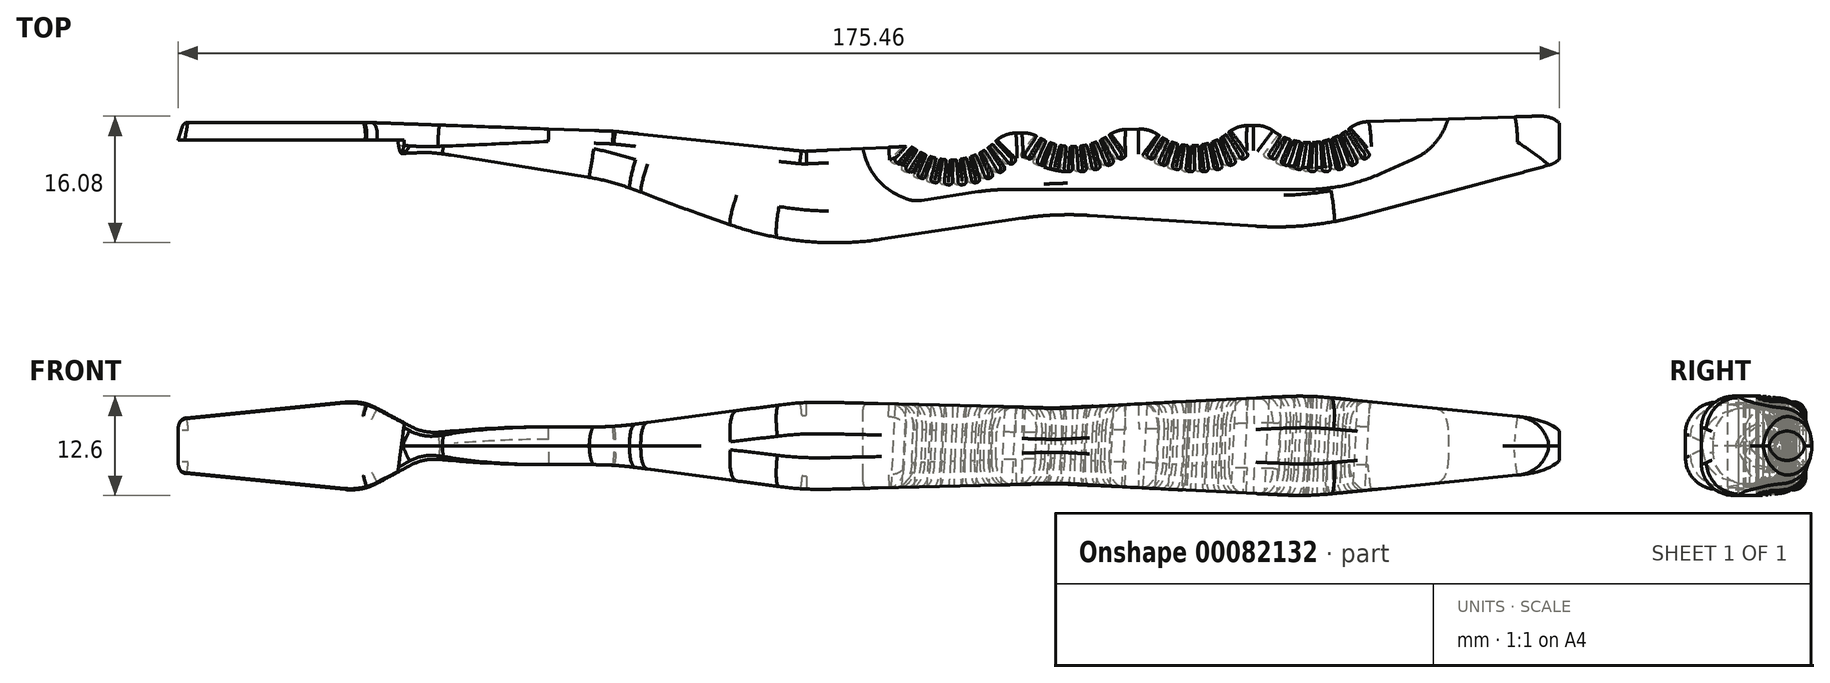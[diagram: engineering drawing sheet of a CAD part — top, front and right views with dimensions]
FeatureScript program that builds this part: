
annotation { "Feature Type Name" : "Feature", "Feature Type Description" : "" }
export const myFeature = defineFeature(function(context is Context, id is Id, definition is map)
    precondition{}
    {
        {
            var Q0;
            Q0=qCreatedBy(makeId("Front.planeOp"),FACE);
            var sketch = newSketch(context, id + "F0", { "sketchPlane" : qUnion([Q0])});
            skLineSegment(sketch, "E0", {"start": v(0, 0) * mm, "end": v(-220, 0) * mm, "construction": true});
            skLineSegment(sketch, "E1", {"start": v(-220, 0) * mm, "end": v(-220, 5) * mm});
            skLineSegment(sketch, "E2", {"start": v(-190, 0) * mm, "end": v(-190, 8) * mm, "construction": true});
            skLineSegment(sketch, "E3", {"start": v(-180, 0) * mm, "end": v(-180, 3) * mm, "construction": true});
            skLineSegment(sketch, "E4", {"start": v(-150, 0) * mm, "end": v(-150, 3) * mm, "construction": true});
            skLineSegment(sketch, "E5", {"start": v(-120, 0) * mm, "end": v(-120, 7) * mm, "construction": true});
            skLineSegment(sketch, "E6", {"start": v(-80, 0) * mm, "end": v(-80, 6) * mm, "construction": true});
            skLineSegment(sketch, "E7", {"start": v(-40, 0) * mm, "end": v(-40, 8) * mm, "construction": true});
            skLineSegment(sketch, "E8", {"start": v(0, 0) * mm, "end": v(0, 4) * mm});
            skLineSegment(sketch, "E9", {"start": v(0, 4) * mm, "end": v(-40, 8) * mm});
            skLineSegment(sketch, "E10", {"start": v(-40, 8) * mm, "end": v(-80, 6) * mm});
            skLineSegment(sketch, "E11", {"start": v(-80, 6) * mm, "end": v(-120, 7) * mm});
            skLineSegment(sketch, "E12", {"start": v(-120, 7) * mm, "end": v(-150, 3) * mm});
            skLineSegment(sketch, "E13", {"start": v(-150, 3) * mm, "end": v(-180, 3) * mm});
            skLineSegment(sketch, "E14", {"start": v(-180, 3) * mm, "end": v(-190, 8) * mm});
            skLineSegment(sketch, "E15", {"start": v(-190, 8) * mm, "end": v(-220, 5) * mm});
            skLineSegment(sketch, "E16.MirrorCS", {"start": v(0, 0) * mm, "end": v(0, -4) * mm});
            skLineSegment(sketch, "E17.MirrorCS", {"start": v(-220, 0) * mm, "end": v(-220, -5) * mm});
            skLineSegment(sketch, "E18.MirrorCS", {"start": v(-190, -8) * mm, "end": v(-220, -5) * mm});
            skLineSegment(sketch, "E19.MirrorCS", {"start": v(-180, -3) * mm, "end": v(-190, -8) * mm});
            skLineSegment(sketch, "E20.MirrorCS", {"start": v(-150, -3) * mm, "end": v(-180, -3) * mm});
            skLineSegment(sketch, "E21.MirrorCS", {"start": v(-120, -7) * mm, "end": v(-150, -3) * mm});
            skLineSegment(sketch, "E22.MirrorCS", {"start": v(-80, -6) * mm, "end": v(-120, -7) * mm});
            skLineSegment(sketch, "E23.MirrorCS", {"start": v(0, -4) * mm, "end": v(-40, -8) * mm});
            skLineSegment(sketch, "E24.MirrorCS", {"start": v(-40, -8) * mm, "end": v(-80, -6) * mm});
            skSolve(sketch);
        }
        {
            var Q0;
            Q0=makeQuery(id+"F0.imprint","IMPRINT",FACE,{"disambiguationData":[TD([[makeQuery(id+"F0.imprint","IMPRINT",EDGE,{"derivedFrom":sQuery(id+"F0.wireOp",EDGE,"E1")}),-1.0]])]});
            extrude(context, id + "F1", {"entities" : qUnion([Q0]), "depth" : 25 * mm});
        }
        {
            var Q0;
            Q0=makeQuery(id+"F1.opExtrude","SWEPT_FACE",FACE,{"disambiguationData":[OSD([sQuery(id+"F0.wireOp",EDGE,"E20.MirrorCS")])]});
            var sketch = newSketch(context, id + "F2", { "sketchPlane" : qUnion([Q0])});
            skLineSegment(sketch, "E25.0", {"start": v(-190, 0) * mm, "end": v(-220, 0) * mm, "construction": true});
            skLineSegment(sketch, "E25.4", {"start": v(-80, 0) * mm, "end": v(-120, 0) * mm, "construction": true});
            skLineSegment(sketch, "E25.5", {"start": v(-40, 0) * mm, "end": v(-80, 0) * mm, "construction": true});
            skLineSegment(sketch, "E25.6", {"start": v(0, 0) * mm, "end": v(-40, 0) * mm, "construction": true});
            skLineSegment(sketch, "E26", {"start": v(-220, 7.68) * mm, "end": v(-218.46, 2.68) * mm});
            skLineSegment(sketch, "E27", {"start": v(-218.46, 2.68) * mm, "end": v(-190, 2.68) * mm});
            skLineSegment(sketch, "E28", {"start": v(-119.9, 7.3) * mm, "end": v(-102.9, 6.47) * mm});
            skLineSegment(sketch, "E29", {"start": v(-119.9, 23.1) * mm, "end": v(-80, 17.11) * mm});
            skLineSegment(sketch, "E30", {"start": v(-80, 17.11) * mm, "end": v(-40, 19.71) * mm});
            skLineSegment(sketch, "E31", {"start": v(-40, 19.71) * mm, "end": v(0, 9.1) * mm});
            skLineSegment(sketch, "E32", {"start": v(0, 9.1) * mm, "end": v(0, 1.58) * mm});
            skArc(sketch, "E33", {"start": v(-88.51, 4.45) * mm, "mid": v(-95.27, 8.57) * mm, "end": v(-102.9, 6.47) * mm});
            skArc(sketch, "E34", {"start": v(-32.26, 2.63) * mm, "mid": v(-39.34, 5.9) * mm, "end": v(-46.62, 3.1) * mm});
            skLineSegment(sketch, "E35", {"start": v(-88.51, 4.45) * mm, "end": v(-83.73, 4.3) * mm});
            skLineSegment(sketch, "E36", {"start": v(-70.5, 3.87) * mm, "end": v(-64.85, 3.69) * mm});
            skArc(sketch, "E37.trimOffspring", {"start": v(-70.5, 3.87) * mm, "mid": v(-77.03, 6.54) * mm, "end": v(-83.73, 4.3) * mm});
            skLineSegment(sketch, "E38.trimOffspring", {"start": v(-51.47, 3.25) * mm, "end": v(-46.62, 3.1) * mm});
            skLineSegment(sketch, "E39.trimOffspring", {"start": v(-32.26, 2.63) * mm, "end": v(0, 1.58) * mm});
            skArc(sketch, "E40.trimOffspring", {"start": v(-51.47, 3.25) * mm, "mid": v(-58.07, 6.39) * mm, "end": v(-64.85, 3.69) * mm});
            skPoint(sketch, "E41.center.orphan", {"position": v(-77.66, -2.25) * mm});
            skPoint(sketch, "E42.center.orphan", {"position": v(-58.66, -3.17) * mm});
            skLineSegment(sketch, "E43.top", {"start": v(-229.41, 31.75) * mm, "end": v(15.55, 31.75) * mm});
            skLineSegment(sketch, "E43.left", {"start": v(-229.41, -17.07) * mm, "end": v(-229.41, 31.75) * mm});
            skLineSegment(sketch, "E43.right", {"start": v(15.55, -17.07) * mm, "end": v(15.55, 31.75) * mm});
            skLineSegment(sketch, "E44", {"start": v(-220, 7.68) * mm, "end": v(-180, 7.68) * mm});
            skLineSegment(sketch, "E45", {"start": v(-180, 7.68) * mm, "end": v(-150, 12.5) * mm});
            skLineSegment(sketch, "E46", {"start": v(-150, 12.5) * mm, "end": v(-119.9, 23.1) * mm});
            skLineSegment(sketch, "E47", {"start": v(-119.9, 7.3) * mm, "end": v(-150, 4.12) * mm});
            skLineSegment(sketch, "E48", {"start": v(-150, 4.12) * mm, "end": v(-190, 2.68) * mm});
            skLineSegment(sketch, "E49", {"start": v(15.55, -17.07) * mm, "end": v(-229.41, -17.07) * mm});
            skSolve(sketch);
        }
        {
            var Q0;
            Q0=makeQuery(id+"F2.imprint","IMPRINT",FACE,{"disambiguationData":[TD([[makeQuery(id+"F2.imprint","IMPRINT",EDGE,{"derivedFrom":sQuery(id+"F2.wireOp",EDGE,"E26")}),-1.0]])]});
            var Q1;
            {var subQ0=sQuery(id+"F2.wireOp",EDGE,"E45");Q1=makeQuery(id+"F2.imprint","IMPRINT",FACE,{"disambiguationData":[TD([[makeQuery(id+"F2.imprint","IMPRINT",EDGE,{"derivedFrom":subQ0}),1.0]])]});}
            var Q2;
            {var subQ1=sQuery(id+"F0.wireOp",EDGE,"E20.MirrorCS");var subQ6=makeQuery(id+"F1.opExtrude","CAP_EDGE",EDGE,{"disambiguationData":[OSD([subQ1])],"isStart":true});Q2=makeQuery(id+"F2.imprint","IMPRINT",FACE,{"disambiguationData":[TD([[makeQuery(id+"F2.imprint","IMPRINT",EDGE,{"derivedFrom":subQ6}),-1.0]])]});}
            extrude(context, id + "F3", {"entities" : qUnion([Q0, Q1, Q2]), "operationType" : NewBodyOperationType.REMOVE, "endBound" : BoundingType.SYMMETRIC, "oppositeDirection" : true, "depth" : 40 * mm});
        }
        {
            var Q0;
            Q0=makeQuery(id+"F3.boolean.opBoolean","COPY",EDGE,{"derivedFrom":makeQuery(id+"F3.opExtrude","SWEPT_EDGE",EDGE,{"disambiguationData":[OSD([sQuery(id+"F2.wireOp",EDGE,"E29"),sQuery(id+"F2.wireOp",EDGE,"E46")])]})});
            var Q1;
            Q1=makeQuery(id+"F3.boolean.opBoolean","COPY",EDGE,{"derivedFrom":makeQuery(id+"F3.opExtrude","SWEPT_EDGE",EDGE,{"disambiguationData":[OSD([sQuery(id+"F2.wireOp",EDGE,"E29"),sQuery(id+"F2.wireOp",EDGE,"E30")])]})});
            var Q2;
            Q2=makeQuery(id+"F3.boolean.opBoolean","COPY",EDGE,{"derivedFrom":makeQuery(id+"F3.opExtrude","SWEPT_EDGE",EDGE,{"disambiguationData":[OSD([sQuery(id+"F2.wireOp",EDGE,"E30"),sQuery(id+"F2.wireOp",EDGE,"E31")])]})});
            var Q3;
            Q3=makeQuery(id+"F3.boolean.opBoolean","COPY",EDGE,{"derivedFrom":makeQuery(id+"F3.opExtrude","SWEPT_EDGE",EDGE,{"disambiguationData":[OSD([sQuery(id+"F0.wireOp",EDGE,"E20.MirrorCS"),sQuery(id+"F0.wireOp",EDGE,"E21.MirrorCS"),sQuery(id+"F2.wireOp",EDGE,"E45"),sQuery(id+"F2.wireOp",EDGE,"E46")])]})});
            var Q4;
            Q4=makeQuery(id+"F3.boolean.opBoolean","COPY",EDGE,{"derivedFrom":makeQuery(id+"F3.opExtrude","SWEPT_EDGE",EDGE,{"disambiguationData":[OSD([sQuery(id+"F0.wireOp",EDGE,"E19.MirrorCS"),sQuery(id+"F0.wireOp",EDGE,"E20.MirrorCS"),sQuery(id+"F2.wireOp",EDGE,"E44"),sQuery(id+"F2.wireOp",EDGE,"E45")])]})});
            fillet(context, id + "F4", {"entities" : qUnion([Q0, Q1, Q2, Q3, Q4]), "radius" : 50 * mm, "tangentPropagation" : true, "allowEdgeOverflow" : false});
        }
        {
            var Q0;
            Q0=makeQuery(id+"F3.boolean.opBoolean","COPY",EDGE,{"derivedFrom":makeQuery(id+"F3.opExtrude","SWEPT_EDGE",EDGE,{"disambiguationData":[OSD([sQuery(id+"F2.wireOp",EDGE,"E27"),sQuery(id+"F2.wireOp",EDGE,"E48")])]})});
            var Q1;
            Q1=makeQuery(id+"F3.boolean.opBoolean","COPY",EDGE,{"derivedFrom":makeQuery(id+"F3.opExtrude","SWEPT_EDGE",EDGE,{"disambiguationData":[OSD([sQuery(id+"F0.wireOp",EDGE,"E20.MirrorCS"),sQuery(id+"F0.wireOp",EDGE,"E21.MirrorCS"),sQuery(id+"F2.wireOp",EDGE,"E47"),sQuery(id+"F2.wireOp",EDGE,"E48")])]})});
            var Q2;
            Q2=makeQuery(id+"F3.boolean.opBoolean","COPY",EDGE,{"derivedFrom":makeQuery(id+"F3.opExtrude","SWEPT_EDGE",EDGE,{"disambiguationData":[OSD([sQuery(id+"F2.wireOp",EDGE,"E28"),sQuery(id+"F2.wireOp",EDGE,"E47")])]})});
            fillet(context, id + "F5", {"entities" : qUnion([Q0, Q1, Q2]), "radius" : 5 * mm, "tangentPropagation" : true, "allowEdgeOverflow" : false});
        }
        {
            var Q0;
            Q0=makeQuery(id+"F1.opExtrude","SWEPT_EDGE",EDGE,{"disambiguationData":[OSD([sQuery(id+"F0.wireOp",EDGE,"E20.MirrorCS"),sQuery(id+"F0.wireOp",EDGE,"E21.MirrorCS")])]});
            var Q1;
            Q1=makeQuery(id+"F1.opExtrude","SWEPT_EDGE",EDGE,{"disambiguationData":[OSD([sQuery(id+"F0.wireOp",EDGE,"E21.MirrorCS"),sQuery(id+"F0.wireOp",EDGE,"E22.MirrorCS")])]});
            var Q2;
            Q2=makeQuery(id+"F1.opExtrude","SWEPT_EDGE",EDGE,{"disambiguationData":[OSD([sQuery(id+"F0.wireOp",EDGE,"E22.MirrorCS"),sQuery(id+"F0.wireOp",EDGE,"E24.MirrorCS")])]});
            var Q3;
            Q3=makeQuery(id+"F1.opExtrude","SWEPT_EDGE",EDGE,{"disambiguationData":[OSD([sQuery(id+"F0.wireOp",EDGE,"E23.MirrorCS"),sQuery(id+"F0.wireOp",EDGE,"E24.MirrorCS")])]});
            var Q4;
            Q4=makeQuery(id+"F1.opExtrude","SWEPT_EDGE",EDGE,{"disambiguationData":[OSD([sQuery(id+"F0.wireOp",EDGE,"E12"),sQuery(id+"F0.wireOp",EDGE,"E13")])]});
            var Q5;
            Q5=makeQuery(id+"F1.opExtrude","SWEPT_EDGE",EDGE,{"disambiguationData":[OSD([sQuery(id+"F0.wireOp",EDGE,"E11"),sQuery(id+"F0.wireOp",EDGE,"E12")])]});
            var Q6;
            Q6=makeQuery(id+"F1.opExtrude","SWEPT_EDGE",EDGE,{"disambiguationData":[OSD([sQuery(id+"F0.wireOp",EDGE,"E10"),sQuery(id+"F0.wireOp",EDGE,"E11")])]});
            var Q7;
            Q7=makeQuery(id+"F1.opExtrude","SWEPT_EDGE",EDGE,{"disambiguationData":[OSD([sQuery(id+"F0.wireOp",EDGE,"E9"),sQuery(id+"F0.wireOp",EDGE,"E10")])]});
            fillet(context, id + "F6", {"entities" : qUnion([Q0, Q1, Q2, Q3, Q4, Q5, Q6, Q7]), "radius" : 50 * mm, "tangentPropagation" : true, "allowEdgeOverflow" : false});
        }
        {
            var Q0;
            Q0=makeQuery(id+"F1.opExtrude","SWEPT_EDGE",EDGE,{"disambiguationData":[OSD([sQuery(id+"F0.wireOp",EDGE,"E18.MirrorCS"),sQuery(id+"F0.wireOp",EDGE,"E19.MirrorCS")])]});
            var Q1;
            Q1=makeQuery(id+"F1.opExtrude","SWEPT_EDGE",EDGE,{"disambiguationData":[OSD([sQuery(id+"F0.wireOp",EDGE,"E19.MirrorCS"),sQuery(id+"F0.wireOp",EDGE,"E20.MirrorCS")])]});
            var Q2;
            Q2=makeQuery(id+"F1.opExtrude","SWEPT_EDGE",EDGE,{"disambiguationData":[OSD([sQuery(id+"F0.wireOp",EDGE,"E13"),sQuery(id+"F0.wireOp",EDGE,"E14")])]});
            var Q3;
            Q3=makeQuery(id+"F1.opExtrude","SWEPT_EDGE",EDGE,{"disambiguationData":[OSD([sQuery(id+"F0.wireOp",EDGE,"E14"),sQuery(id+"F0.wireOp",EDGE,"E15")])]});
            fillet(context, id + "F7", {"entities" : qUnion([Q0, Q1, Q2, Q3]), "radius" : 10 * mm, "tangentPropagation" : true, "allowEdgeOverflow" : false});
        }
        {
            var Q0;
            Q0=makeQuery(id+"F6.opFillet","BLEND_EDGE",EDGE,{"blendedFrom":[makeQuery(id+"F1.opExtrude","SWEPT_EDGE",EDGE,{"disambiguationData":[OSD([sQuery(id+"F0.wireOp",EDGE,"E21.MirrorCS"),sQuery(id+"F0.wireOp",EDGE,"E22.MirrorCS")])]}),makeQuery(id+"F4.opFillet","BLEND_FACE",FACE,{"disambiguationData":[OSD([sQuery(id+"F2.wireOp",EDGE,"E29"),sQuery(id+"F2.wireOp",EDGE,"E46")])]})],"blendedInto":[makeQuery(id+"F4.opFillet","BLEND_FACE",FACE,{"disambiguationData":[OSD([sQuery(id+"F2.wireOp",EDGE,"E29"),sQuery(id+"F2.wireOp",EDGE,"E46")])]})]});
            var Q1;
            Q1=makeQuery(id+"F3.boolean.opBoolean","INTERSECT",EDGE,{"derivedFrom":[makeQuery(id+"F1.opExtrude","SWEPT_FACE",FACE,{"disambiguationData":[OSD([sQuery(id+"F0.wireOp",EDGE,"E11")])]}),makeQuery(id+"F3.opExtrude","SWEPT_FACE",FACE,{"disambiguationData":[OSD([sQuery(id+"F2.wireOp",EDGE,"E29")])]})]});
            fillet(context, id + "F8", {"entities" : qUnion([Q0, Q1]), "radius" : 5 * mm, "tangentPropagation" : true, "allowEdgeOverflow" : false});
        }
        {
            var Q0;
            Q0=makeQuery(id+"F3.boolean.opBoolean","INTERSECT",EDGE,{"derivedFrom":[makeQuery(id+"F1.opExtrude","SWEPT_FACE",FACE,{"disambiguationData":[OSD([sQuery(id+"F0.wireOp",EDGE,"E22.MirrorCS")])]}),makeQuery(id+"F3.opExtrude","SWEPT_FACE",FACE,{"disambiguationData":[OSD([sQuery(id+"F2.wireOp",EDGE,"E33")])]})]});
            var Q1;
            Q1=makeQuery(id+"F6.opFillet","BLEND_EDGE",EDGE,{"blendedFrom":[makeQuery(id+"F1.opExtrude","SWEPT_EDGE",EDGE,{"disambiguationData":[OSD([sQuery(id+"F0.wireOp",EDGE,"E22.MirrorCS"),sQuery(id+"F0.wireOp",EDGE,"E24.MirrorCS")])]}),makeQuery(id+"F3.boolean.opBoolean","COPY",FACE,{"derivedFrom":makeQuery(id+"F3.opExtrude","SWEPT_FACE",FACE,{"disambiguationData":[OSD([sQuery(id+"F2.wireOp",EDGE,"E37.trimOffspring")])]})})],"blendedInto":[makeQuery(id+"F3.boolean.opBoolean","COPY",FACE,{"derivedFrom":makeQuery(id+"F3.opExtrude","SWEPT_FACE",FACE,{"disambiguationData":[OSD([sQuery(id+"F2.wireOp",EDGE,"E37.trimOffspring")])]})})]});
            var Q2;
            Q2=makeQuery(id+"F3.boolean.opBoolean","INTERSECT",EDGE,{"derivedFrom":[makeQuery(id+"F1.opExtrude","SWEPT_FACE",FACE,{"disambiguationData":[OSD([sQuery(id+"F0.wireOp",EDGE,"E24.MirrorCS")])]}),makeQuery(id+"F3.opExtrude","SWEPT_FACE",FACE,{"disambiguationData":[OSD([sQuery(id+"F2.wireOp",EDGE,"E40.trimOffspring")])]})]});
            var Q3;
            Q3=makeQuery(id+"F6.opFillet","BLEND_EDGE",EDGE,{"blendedFrom":[makeQuery(id+"F1.opExtrude","SWEPT_EDGE",EDGE,{"disambiguationData":[OSD([sQuery(id+"F0.wireOp",EDGE,"E23.MirrorCS"),sQuery(id+"F0.wireOp",EDGE,"E24.MirrorCS")])]}),makeQuery(id+"F3.boolean.opBoolean","COPY",FACE,{"derivedFrom":makeQuery(id+"F3.opExtrude","SWEPT_FACE",FACE,{"disambiguationData":[OSD([sQuery(id+"F2.wireOp",EDGE,"E34")])]})})],"blendedInto":[makeQuery(id+"F3.boolean.opBoolean","COPY",FACE,{"derivedFrom":makeQuery(id+"F3.opExtrude","SWEPT_FACE",FACE,{"disambiguationData":[OSD([sQuery(id+"F2.wireOp",EDGE,"E34")])]})})]});
            var Q4;
            Q4=makeQuery(id+"F3.boolean.opBoolean","INTERSECT",EDGE,{"derivedFrom":[makeQuery(id+"F1.opExtrude","SWEPT_FACE",FACE,{"disambiguationData":[OSD([sQuery(id+"F0.wireOp",EDGE,"E22.MirrorCS")])]}),makeQuery(id+"F3.opExtrude","SWEPT_FACE",FACE,{"disambiguationData":[OSD([sQuery(id+"F2.wireOp",EDGE,"E35")])]})]});
            var Q5;
            Q5=makeQuery(id+"F3.boolean.opBoolean","INTERSECT",EDGE,{"derivedFrom":[makeQuery(id+"F1.opExtrude","SWEPT_FACE",FACE,{"disambiguationData":[OSD([sQuery(id+"F0.wireOp",EDGE,"E24.MirrorCS")])]}),makeQuery(id+"F3.opExtrude","SWEPT_FACE",FACE,{"disambiguationData":[OSD([sQuery(id+"F2.wireOp",EDGE,"E36")])]})]});
            var Q6;
            Q6=makeQuery(id+"F3.boolean.opBoolean","INTERSECT",EDGE,{"derivedFrom":[makeQuery(id+"F1.opExtrude","SWEPT_FACE",FACE,{"disambiguationData":[OSD([sQuery(id+"F0.wireOp",EDGE,"E24.MirrorCS")])]}),makeQuery(id+"F3.opExtrude","SWEPT_FACE",FACE,{"disambiguationData":[OSD([sQuery(id+"F2.wireOp",EDGE,"E38.trimOffspring")])]})]});
            var Q7;
            Q7=makeQuery(id+"F3.boolean.opBoolean","INTERSECT",EDGE,{"derivedFrom":[makeQuery(id+"F1.opExtrude","SWEPT_FACE",FACE,{"disambiguationData":[OSD([sQuery(id+"F0.wireOp",EDGE,"E23.MirrorCS")])]}),makeQuery(id+"F3.opExtrude","SWEPT_FACE",FACE,{"disambiguationData":[OSD([sQuery(id+"F2.wireOp",EDGE,"E39.trimOffspring")])]})]});
            var Q8;
            Q8=makeQuery(id+"F3.boolean.opBoolean","INTERSECT",EDGE,{"derivedFrom":[makeQuery(id+"F1.opExtrude","SWEPT_FACE",FACE,{"disambiguationData":[OSD([sQuery(id+"F0.wireOp",EDGE,"E11")])]}),makeQuery(id+"F3.opExtrude","SWEPT_FACE",FACE,{"disambiguationData":[OSD([sQuery(id+"F2.wireOp",EDGE,"E33")])]})]});
            var Q9;
            Q9=makeQuery(id+"F3.boolean.opBoolean","INTERSECT",EDGE,{"derivedFrom":[makeQuery(id+"F1.opExtrude","SWEPT_FACE",FACE,{"disambiguationData":[OSD([sQuery(id+"F0.wireOp",EDGE,"E11")])]}),makeQuery(id+"F3.opExtrude","SWEPT_FACE",FACE,{"disambiguationData":[OSD([sQuery(id+"F2.wireOp",EDGE,"E35")])]})]});
            var Q10;
            Q10=makeQuery(id+"F3.boolean.opBoolean","INTERSECT",EDGE,{"derivedFrom":[makeQuery(id+"F1.opExtrude","SWEPT_FACE",FACE,{"disambiguationData":[OSD([sQuery(id+"F0.wireOp",EDGE,"E10")])]}),makeQuery(id+"F3.opExtrude","SWEPT_FACE",FACE,{"disambiguationData":[OSD([sQuery(id+"F2.wireOp",EDGE,"E37.trimOffspring")])]})]});
            var Q11;
            Q11=makeQuery(id+"F3.boolean.opBoolean","INTERSECT",EDGE,{"derivedFrom":[makeQuery(id+"F1.opExtrude","SWEPT_FACE",FACE,{"disambiguationData":[OSD([sQuery(id+"F0.wireOp",EDGE,"E10")])]}),makeQuery(id+"F3.opExtrude","SWEPT_FACE",FACE,{"disambiguationData":[OSD([sQuery(id+"F2.wireOp",EDGE,"E36")])]})]});
            var Q12;
            Q12=makeQuery(id+"F3.boolean.opBoolean","INTERSECT",EDGE,{"derivedFrom":[makeQuery(id+"F1.opExtrude","SWEPT_FACE",FACE,{"disambiguationData":[OSD([sQuery(id+"F0.wireOp",EDGE,"E10")])]}),makeQuery(id+"F3.opExtrude","SWEPT_FACE",FACE,{"disambiguationData":[OSD([sQuery(id+"F2.wireOp",EDGE,"E40.trimOffspring")])]})]});
            var Q13;
            Q13=makeQuery(id+"F3.boolean.opBoolean","INTERSECT",EDGE,{"derivedFrom":[makeQuery(id+"F1.opExtrude","SWEPT_FACE",FACE,{"disambiguationData":[OSD([sQuery(id+"F0.wireOp",EDGE,"E10")])]}),makeQuery(id+"F3.opExtrude","SWEPT_FACE",FACE,{"disambiguationData":[OSD([sQuery(id+"F2.wireOp",EDGE,"E38.trimOffspring")])]})]});
            var Q14;
            Q14=makeQuery(id+"F6.opFillet","BLEND_EDGE",EDGE,{"blendedFrom":[makeQuery(id+"F1.opExtrude","SWEPT_EDGE",EDGE,{"disambiguationData":[OSD([sQuery(id+"F0.wireOp",EDGE,"E9"),sQuery(id+"F0.wireOp",EDGE,"E10")])]}),makeQuery(id+"F3.boolean.opBoolean","COPY",FACE,{"derivedFrom":makeQuery(id+"F3.opExtrude","SWEPT_FACE",FACE,{"disambiguationData":[OSD([sQuery(id+"F2.wireOp",EDGE,"E34")])]})})],"blendedInto":[makeQuery(id+"F3.boolean.opBoolean","COPY",FACE,{"derivedFrom":makeQuery(id+"F3.opExtrude","SWEPT_FACE",FACE,{"disambiguationData":[OSD([sQuery(id+"F2.wireOp",EDGE,"E34")])]})})]});
            var Q15;
            Q15=makeQuery(id+"F3.boolean.opBoolean","INTERSECT",EDGE,{"derivedFrom":[makeQuery(id+"F1.opExtrude","SWEPT_FACE",FACE,{"disambiguationData":[OSD([sQuery(id+"F0.wireOp",EDGE,"E9")])]}),makeQuery(id+"F3.opExtrude","SWEPT_FACE",FACE,{"disambiguationData":[OSD([sQuery(id+"F2.wireOp",EDGE,"E39.trimOffspring")])]})]});
            fillet(context, id + "F9", {"entities" : qUnion([Q0, Q1, Q2, Q3, Q4, Q5, Q6, Q7, Q8, Q9, Q10, Q11, Q12, Q13, Q14, Q15]), "radius" : 4 * mm, "tangentPropagation" : true, "allowEdgeOverflow" : false});
        }
        {
            var Q0;
            Q0=makeQuery(id+"F3.boolean.opBoolean","INTERSECT",EDGE,{"derivedFrom":[makeQuery(id+"F1.opExtrude","SWEPT_FACE",FACE,{"disambiguationData":[OSD([sQuery(id+"F0.wireOp",EDGE,"E22.MirrorCS")])]}),makeQuery(id+"F3.opExtrude","SWEPT_FACE",FACE,{"disambiguationData":[OSD([sQuery(id+"F2.wireOp",EDGE,"E28")])]})]});
            fillet(context, id + "F10", {"entities" : qUnion([Q0]), "radius" : 2 * mm, "tangentPropagation" : true, "allowEdgeOverflow" : false});
        }
        {
            var Q0;
            Q0=makeQuery(id+"F3.boolean.opBoolean","COPY",EDGE,{"derivedFrom":makeQuery(id+"F3.opExtrude","SWEPT_EDGE",EDGE,{"disambiguationData":[OSD([sQuery(id+"F2.wireOp",EDGE,"E33"),sQuery(id+"F2.wireOp",EDGE,"E35")])]})});
            var Q1;
            Q1=makeQuery(id+"F3.boolean.opBoolean","COPY",EDGE,{"derivedFrom":makeQuery(id+"F3.opExtrude","SWEPT_EDGE",EDGE,{"disambiguationData":[OSD([sQuery(id+"F2.wireOp",EDGE,"E35"),sQuery(id+"F2.wireOp",EDGE,"E37.trimOffspring")])]})});
            var Q2;
            Q2=makeQuery(id+"F3.boolean.opBoolean","COPY",EDGE,{"derivedFrom":makeQuery(id+"F3.opExtrude","SWEPT_EDGE",EDGE,{"disambiguationData":[OSD([sQuery(id+"F2.wireOp",EDGE,"E36"),sQuery(id+"F2.wireOp",EDGE,"E37.trimOffspring")])]})});
            var Q3;
            Q3=makeQuery(id+"F3.boolean.opBoolean","COPY",EDGE,{"derivedFrom":makeQuery(id+"F3.opExtrude","SWEPT_EDGE",EDGE,{"disambiguationData":[OSD([sQuery(id+"F2.wireOp",EDGE,"E36"),sQuery(id+"F2.wireOp",EDGE,"E40.trimOffspring")])]})});
            var Q4;
            Q4=makeQuery(id+"F3.boolean.opBoolean","COPY",EDGE,{"derivedFrom":makeQuery(id+"F3.opExtrude","SWEPT_EDGE",EDGE,{"disambiguationData":[OSD([sQuery(id+"F2.wireOp",EDGE,"E38.trimOffspring"),sQuery(id+"F2.wireOp",EDGE,"E40.trimOffspring")])]})});
            var Q5;
            Q5=makeQuery(id+"F3.boolean.opBoolean","COPY",EDGE,{"derivedFrom":makeQuery(id+"F3.opExtrude","SWEPT_EDGE",EDGE,{"disambiguationData":[OSD([sQuery(id+"F2.wireOp",EDGE,"E34"),sQuery(id+"F2.wireOp",EDGE,"E38.trimOffspring")])]})});
            var Q6;
            Q6=makeQuery(id+"F3.boolean.opBoolean","COPY",EDGE,{"derivedFrom":makeQuery(id+"F3.opExtrude","SWEPT_EDGE",EDGE,{"disambiguationData":[OSD([sQuery(id+"F2.wireOp",EDGE,"E34"),sQuery(id+"F2.wireOp",EDGE,"E39.trimOffspring")])]})});
            fillet(context, id + "F11", {"entities" : qUnion([Q0, Q1, Q2, Q3, Q4, Q5, Q6]), "radius" : 5 * mm, "tangentPropagation" : true, "allowEdgeOverflow" : false});
        }
        {
            var Q0;
            Q0=makeQuery(id+"F8.opFillet","BLEND_EDGE",EDGE,{"blendedFrom":[makeQuery(id+"F3.boolean.opBoolean","INTERSECT",EDGE,{"derivedFrom":[makeQuery(id+"F1.opExtrude","SWEPT_FACE",FACE,{"disambiguationData":[OSD([sQuery(id+"F0.wireOp",EDGE,"E18.MirrorCS")])]}),makeQuery(id+"F3.opExtrude","SWEPT_FACE",FACE,{"disambiguationData":[OSD([sQuery(id+"F2.wireOp",EDGE,"E44")])]})]}),makeQuery(id+"F3.boolean.opBoolean","COPY",FACE,{"derivedFrom":makeQuery(id+"F3.opExtrude","SWEPT_FACE",FACE,{"disambiguationData":[OSD([sQuery(id+"F2.wireOp",EDGE,"E26")])]})})],"blendedInto":[makeQuery(id+"F3.boolean.opBoolean","COPY",FACE,{"derivedFrom":makeQuery(id+"F3.opExtrude","SWEPT_FACE",FACE,{"disambiguationData":[OSD([sQuery(id+"F2.wireOp",EDGE,"E26")])]})})]});
            fillet(context, id + "F12", {"entities" : qUnion([Q0]), "radius" : 1 * mm, "tangentPropagation" : true, "allowEdgeOverflow" : false});
        }
        {
            var Q0;
            Q0=qCreatedBy(makeId("Top.planeOp"),FACE);
            var sketch = newSketch(context, id + "F13", { "sketchPlane" : qUnion([Q0])});
            skLineSegment(sketch, "E50", {"start": v(-111.36, -3.91) * mm, "end": v(-110.38, -7.71) * mm});
            skLineSegment(sketch, "E51", {"start": v(-104.93, -14.29) * mm, "end": v(-104.14, -14.66) * mm});
            skLineSegment(sketch, "E52", {"start": v(-101.27, -15.07) * mm, "end": v(-92.35, -13.7) * mm});
            skLineSegment(sketch, "E53", {"start": v(-87.82, -13.36) * mm, "end": v(-74.2, -13.36) * mm});
            skLineSegment(sketch, "E54", {"start": v(-74.2, -13.36) * mm, "end": v(-53.16, -13.36) * mm});
            skLineSegment(sketch, "E55", {"start": v(-53.16, -13.36) * mm, "end": v(-40.43, -13.36) * mm});
            skLineSegment(sketch, "E56", {"start": v(-28.35, -10.83) * mm, "end": v(-23.32, -8.61) * mm});
            skLineSegment(sketch, "E57", {"start": v(-18.04, -3.12) * mm, "end": v(-16.8, 0) * mm});
            skPoint(sketch, "E58.visualSharp", {"position": v(-109.21, -12.29) * mm});
            skArc(sketch, "E58.filletArc", {"start": v(-110.38, -7.71) * mm, "mid": v(-108.4, -11.61) * mm, "end": v(-104.93, -14.29) * mm});
            skPoint(sketch, "E59.visualSharp", {"position": v(-102.77, -15.3) * mm});
            skArc(sketch, "E59.filletArc", {"start": v(-104.14, -14.66) * mm, "mid": v(-102.74, -15.07) * mm, "end": v(-101.27, -15.07) * mm});
            skPoint(sketch, "E60.visualSharp", {"position": v(-19.55, -6.95) * mm});
            skArc(sketch, "E60.filletArc", {"start": v(-23.32, -8.61) * mm, "mid": v(-20.13, -6.39) * mm, "end": v(-18.04, -3.12) * mm});
            skPoint(sketch, "E61.visualSharp", {"position": v(-34.12, -13.36) * mm});
            skArc(sketch, "E61.filletArc", {"start": v(-40.43, -13.36) * mm, "mid": v(-34.26, -12.72) * mm, "end": v(-28.35, -10.83) * mm});
            skPoint(sketch, "E62.visualSharp", {"position": v(-90.1, -13.36) * mm});
            skArc(sketch, "E62.filletArc", {"start": v(-87.82, -13.36) * mm, "mid": v(-90.1, -13.45) * mm, "end": v(-92.35, -13.7) * mm});
            skLineSegment(sketch, "E63", {"start": v(-111.36, -3.91) * mm, "end": v(-16.8, 0) * mm});
            skSolve(sketch);
        }
        {
            var Q0;
            Q0=makeQuery(id+"F13.imprint","IMPRINT",FACE,{"disambiguationData":[TD([[makeQuery(id+"F13.imprint","IMPRINT",EDGE,{"derivedFrom":sQuery(id+"F13.wireOp",EDGE,"E50")}),1.0]])]});
            extrude(context, id + "F14", {"entities" : qUnion([Q0]), "endBound" : BoundingType.SYMMETRIC, "depth" : 40 * mm});
        }
        {
            var Q0;
            Q0=makeQuery(id+"F14.opExtrude","SWEPT_BODY",BODY,{"disambiguationData":[OSD([sQuery(id+"F13.wireOp",EDGE,"E50"),sQuery(id+"F13.wireOp",EDGE,"E51"),sQuery(id+"F13.wireOp",EDGE,"E52"),sQuery(id+"F13.wireOp",EDGE,"E53"),sQuery(id+"F13.wireOp",EDGE,"E54"),sQuery(id+"F13.wireOp",EDGE,"E55"),sQuery(id+"F13.wireOp",EDGE,"E56"),sQuery(id+"F13.wireOp",EDGE,"E57"),sQuery(id+"F13.wireOp",EDGE,"E58.filletArc"),sQuery(id+"F13.wireOp",EDGE,"E59.filletArc"),sQuery(id+"F13.wireOp",EDGE,"E60.filletArc"),sQuery(id+"F13.wireOp",EDGE,"E61.filletArc"),sQuery(id+"F13.wireOp",EDGE,"E62.filletArc"),sQuery(id+"F13.wireOp",EDGE,"E63")])]});
            var Q1;
            Q1=makeQuery(id+"F1.opExtrude","SWEPT_BODY",BODY,{"disambiguationData":[OSD([sQuery(id+"F0.wireOp",EDGE,"E1"),sQuery(id+"F0.wireOp",EDGE,"E8"),sQuery(id+"F0.wireOp",EDGE,"E9"),sQuery(id+"F0.wireOp",EDGE,"E10"),sQuery(id+"F0.wireOp",EDGE,"E11"),sQuery(id+"F0.wireOp",EDGE,"E12"),sQuery(id+"F0.wireOp",EDGE,"E13"),sQuery(id+"F0.wireOp",EDGE,"E14"),sQuery(id+"F0.wireOp",EDGE,"E15"),sQuery(id+"F0.wireOp",EDGE,"E16.MirrorCS"),sQuery(id+"F0.wireOp",EDGE,"E17.MirrorCS"),sQuery(id+"F0.wireOp",EDGE,"E18.MirrorCS"),sQuery(id+"F0.wireOp",EDGE,"E19.MirrorCS"),sQuery(id+"F0.wireOp",EDGE,"E20.MirrorCS"),sQuery(id+"F0.wireOp",EDGE,"E21.MirrorCS"),sQuery(id+"F0.wireOp",EDGE,"E22.MirrorCS"),sQuery(id+"F0.wireOp",EDGE,"E23.MirrorCS"),sQuery(id+"F0.wireOp",EDGE,"E24.MirrorCS")])]});
            booleanBodies(context, id + "F15", {"operationType" : BooleanOperationType.INTERSECTION, "tools" : qUnion([Q0, Q1]), "keepTools" : true});
        }
        {
            var Q0;
            Q0=makeQuery(id+"F15.opBoolean","INTERSECT",BODY,{"derivedFrom":[makeQuery(id+"F1.opExtrude","SWEPT_BODY",BODY,{"disambiguationData":[OSD([sQuery(id+"F0.wireOp",EDGE,"E1"),sQuery(id+"F0.wireOp",EDGE,"E8"),sQuery(id+"F0.wireOp",EDGE,"E9"),sQuery(id+"F0.wireOp",EDGE,"E10"),sQuery(id+"F0.wireOp",EDGE,"E11"),sQuery(id+"F0.wireOp",EDGE,"E12"),sQuery(id+"F0.wireOp",EDGE,"E13"),sQuery(id+"F0.wireOp",EDGE,"E14"),sQuery(id+"F0.wireOp",EDGE,"E15"),sQuery(id+"F0.wireOp",EDGE,"E16.MirrorCS"),sQuery(id+"F0.wireOp",EDGE,"E17.MirrorCS"),sQuery(id+"F0.wireOp",EDGE,"E18.MirrorCS"),sQuery(id+"F0.wireOp",EDGE,"E19.MirrorCS"),sQuery(id+"F0.wireOp",EDGE,"E20.MirrorCS"),sQuery(id+"F0.wireOp",EDGE,"E21.MirrorCS"),sQuery(id+"F0.wireOp",EDGE,"E22.MirrorCS"),sQuery(id+"F0.wireOp",EDGE,"E23.MirrorCS"),sQuery(id+"F0.wireOp",EDGE,"E24.MirrorCS")])]}),makeQuery(id+"F14.opExtrude","SWEPT_BODY",BODY,{"disambiguationData":[OSD([sQuery(id+"F13.wireOp",EDGE,"E50"),sQuery(id+"F13.wireOp",EDGE,"E51"),sQuery(id+"F13.wireOp",EDGE,"E52"),sQuery(id+"F13.wireOp",EDGE,"E53"),sQuery(id+"F13.wireOp",EDGE,"E54"),sQuery(id+"F13.wireOp",EDGE,"E55"),sQuery(id+"F13.wireOp",EDGE,"E56"),sQuery(id+"F13.wireOp",EDGE,"E57"),sQuery(id+"F13.wireOp",EDGE,"E58.filletArc"),sQuery(id+"F13.wireOp",EDGE,"E59.filletArc"),sQuery(id+"F13.wireOp",EDGE,"E60.filletArc"),sQuery(id+"F13.wireOp",EDGE,"E61.filletArc"),sQuery(id+"F13.wireOp",EDGE,"E62.filletArc"),sQuery(id+"F13.wireOp",EDGE,"E63")])]})]});
            var Q1;
            Q1=makeQuery(id+"F1.opExtrude","SWEPT_BODY",BODY,{"disambiguationData":[OSD([sQuery(id+"F0.wireOp",EDGE,"E1"),sQuery(id+"F0.wireOp",EDGE,"E8"),sQuery(id+"F0.wireOp",EDGE,"E9"),sQuery(id+"F0.wireOp",EDGE,"E10"),sQuery(id+"F0.wireOp",EDGE,"E11"),sQuery(id+"F0.wireOp",EDGE,"E12"),sQuery(id+"F0.wireOp",EDGE,"E13"),sQuery(id+"F0.wireOp",EDGE,"E14"),sQuery(id+"F0.wireOp",EDGE,"E15"),sQuery(id+"F0.wireOp",EDGE,"E16.MirrorCS"),sQuery(id+"F0.wireOp",EDGE,"E17.MirrorCS"),sQuery(id+"F0.wireOp",EDGE,"E18.MirrorCS"),sQuery(id+"F0.wireOp",EDGE,"E19.MirrorCS"),sQuery(id+"F0.wireOp",EDGE,"E20.MirrorCS"),sQuery(id+"F0.wireOp",EDGE,"E21.MirrorCS"),sQuery(id+"F0.wireOp",EDGE,"E22.MirrorCS"),sQuery(id+"F0.wireOp",EDGE,"E23.MirrorCS"),sQuery(id+"F0.wireOp",EDGE,"E24.MirrorCS")])]});
            booleanBodies(context, id + "F16", {"operationType" : BooleanOperationType.SUBTRACTION, "tools" : qUnion([Q0]), "targets" : qUnion([Q1]), "keepTools" : true});
        }
        {
            var Q0;
            Q0=makeQuery(id+"F15.opBoolean","COPY",FACE,{"derivedFrom":makeQuery(id+"F1.opExtrude","SWEPT_FACE",FACE,{"disambiguationData":[OSD([sQuery(id+"F0.wireOp",EDGE,"E24.MirrorCS")])]})});
            var sketch = newSketch(context, id + "F17", { "sketchPlane" : qUnion([Q0])});
            skEllipticalArc(sketch, "E64.0", {});
            skLineSegment(sketch, "E65", {"start": v(-96.12, -1.34) * mm, "end": v(-105.56, 8.28) * mm});
            skLineSegment(sketch, "E66", {"start": v(-96.12, -1.34) * mm, "end": v(-104.6, 9.15) * mm});
            skLineSegment(sketch, "E67.anchor1", {"start": v(-96.12, -1.34) * mm, "end": v(-96.12, -1.34) * mm});
            skLineSegment(sketch, "E67.anchor2", {"start": v(-96.12, -1.34) * mm, "end": v(-96.12, -1.34) * mm});
            skPoint(sketch, "E68.visualSharp", {"position": v(-104.91, 9.54) * mm});
            skArc(sketch, "E68.filletArc", {"start": v(-104.6, 9.15) * mm, "mid": v(-104.94, 9.33) * mm, "end": v(-105.31, 9.2) * mm});
            skPoint(sketch, "E69.visualSharp", {"position": v(-105.91, 8.65) * mm});
            skArc(sketch, "E69.filletArc", {"start": v(-105.54, 9) * mm, "mid": v(-105.7, 8.65) * mm, "end": v(-105.56, 8.28) * mm});
            skLineSegment(sketch, "E70.1.0", {"start": v(-96.12, -1.34) * mm, "end": v(-102.8, 10.37) * mm});
            skLineSegment(sketch, "E70.1.1", {"start": v(-96.12, -1.34) * mm, "end": v(-103.89, 9.68) * mm});
            skArc(sketch, "E70.1.2", {"start": v(-102.8, 10.37) * mm, "mid": v(-103.1, 10.6) * mm, "end": v(-103.5, 10.55) * mm});
            skEllipticalArc(sketch, "E70.1.3", {});
            skArc(sketch, "E70.1.4", {"start": v(-103.75, 10.38) * mm, "mid": v(-103.97, 10.06) * mm, "end": v(-103.89, 9.68) * mm});
            skLineSegment(sketch, "E70.2.0", {"start": v(-96.12, -1.34) * mm, "end": v(-100.83, 11.3) * mm});
            skLineSegment(sketch, "E70.2.1", {"start": v(-96.12, -1.34) * mm, "end": v(-102.01, 10.78) * mm});
            skArc(sketch, "E70.2.2", {"start": v(-100.83, 11.3) * mm, "mid": v(-101.1, 11.58) * mm, "end": v(-101.49, 11.58) * mm});
            skEllipticalArc(sketch, "E70.2.3", {});
            skArc(sketch, "E70.2.4", {"start": v(-101.77, 11.46) * mm, "mid": v(-102.03, 11.17) * mm, "end": v(-102.01, 10.78) * mm});
            skLineSegment(sketch, "E70.3.0", {"start": v(-96.12, -1.34) * mm, "end": v(-98.73, 11.88) * mm});
            skLineSegment(sketch, "E70.3.1", {"start": v(-96.12, -1.34) * mm, "end": v(-99.99, 11.57) * mm});
            skArc(sketch, "E70.3.2", {"start": v(-98.73, 11.88) * mm, "mid": v(-98.95, 12.2) * mm, "end": v(-99.34, 12.27) * mm});
            skEllipticalArc(sketch, "E70.3.3", {});
            skArc(sketch, "E70.3.4", {"start": v(-99.64, 12.2) * mm, "mid": v(-99.94, 11.96) * mm, "end": v(-99.99, 11.57) * mm});
            skLineSegment(sketch, "E70.4.0", {"start": v(-96.12, -1.34) * mm, "end": v(-96.57, 12.13) * mm});
            skLineSegment(sketch, "E70.4.1", {"start": v(-96.12, -1.34) * mm, "end": v(-97.86, 12.03) * mm});
            skArc(sketch, "E70.4.2", {"start": v(-96.57, 12.13) * mm, "mid": v(-96.74, 12.49) * mm, "end": v(-97.1, 12.61) * mm});
            skEllipticalArc(sketch, "E70.4.3", {});
            skArc(sketch, "E70.4.4", {"start": v(-97.41, 12.59) * mm, "mid": v(-97.76, 12.4) * mm, "end": v(-97.86, 12.03) * mm});
            skLineSegment(sketch, "E70.5.0", {"start": v(-96.12, -1.34) * mm, "end": v(-94.4, 12.03) * mm});
            skLineSegment(sketch, "E70.5.1", {"start": v(-96.12, -1.34) * mm, "end": v(-95.69, 12.13) * mm});
            skArc(sketch, "E70.5.2", {"start": v(-94.4, 12.03) * mm, "mid": v(-94.5, 12.4) * mm, "end": v(-94.85, 12.6) * mm});
            skEllipticalArc(sketch, "E70.5.3", {});
            skArc(sketch, "E70.5.4", {"start": v(-95.16, 12.61) * mm, "mid": v(-95.52, 12.49) * mm, "end": v(-95.69, 12.13) * mm});
            skLineSegment(sketch, "E70.6.0", {"start": v(-96.12, -1.34) * mm, "end": v(-92.27, 11.58) * mm});
            skLineSegment(sketch, "E70.6.1", {"start": v(-96.12, -1.34) * mm, "end": v(-93.53, 11.89) * mm});
            skArc(sketch, "E70.6.2", {"start": v(-92.27, 11.58) * mm, "mid": v(-92.32, 11.97) * mm, "end": v(-92.63, 12.2) * mm});
            skEllipticalArc(sketch, "E70.6.3", {});
            skArc(sketch, "E70.6.4", {"start": v(-92.92, 12.28) * mm, "mid": v(-93.3, 12.21) * mm, "end": v(-93.53, 11.89) * mm});
            skLineSegment(sketch, "E70.7.0", {"start": v(-96.12, -1.34) * mm, "end": v(-90.24, 10.8) * mm});
            skLineSegment(sketch, "E70.7.1", {"start": v(-96.12, -1.34) * mm, "end": v(-91.43, 11.3) * mm});
            skArc(sketch, "E70.7.2", {"start": v(-90.24, 10.8) * mm, "mid": v(-90.23, 11.18) * mm, "end": v(-90.5, 11.47) * mm});
            skEllipticalArc(sketch, "E70.7.3", {});
            skArc(sketch, "E70.7.4", {"start": v(-90.78, 11.59) * mm, "mid": v(-91.17, 11.58) * mm, "end": v(-91.43, 11.3) * mm});
            skLineSegment(sketch, "E70.8.0", {"start": v(-96.12, -1.34) * mm, "end": v(-88.37, 9.69) * mm});
            skLineSegment(sketch, "E70.8.1", {"start": v(-96.12, -1.34) * mm, "end": v(-89.46, 10.38) * mm});
            skArc(sketch, "E70.8.2", {"start": v(-88.37, 9.69) * mm, "mid": v(-88.29, 10.07) * mm, "end": v(-88.5, 10.4) * mm});
            skEllipticalArc(sketch, "E70.8.3", {});
            skArc(sketch, "E70.8.4", {"start": v(-88.77, 10.56) * mm, "mid": v(-89.15, 10.62) * mm, "end": v(-89.46, 10.38) * mm});
            skLineSegment(sketch, "E70.9.0", {"start": v(-96.12, -1.34) * mm, "end": v(-86.7, 8.3) * mm});
            skLineSegment(sketch, "E70.9.1", {"start": v(-96.12, -1.34) * mm, "end": v(-87.67, 9.15) * mm});
            skArc(sketch, "E70.9.2", {"start": v(-86.7, 8.3) * mm, "mid": v(-86.56, 8.66) * mm, "end": v(-86.72, 9.02) * mm});
            skEllipticalArc(sketch, "E70.9.3", {});
            skArc(sketch, "E70.9.4", {"start": v(-86.95, 9.22) * mm, "mid": v(-87.32, 9.34) * mm, "end": v(-87.67, 9.15) * mm});
            skPoint(sketch, "E71.center", {"position": v(-77.09, -3.64) * mm});
            skLineSegment(sketch, "E71.anchor1", {"start": v(-77.09, -3.64) * mm, "end": v(-77.09, -3.64) * mm});
            skLineSegment(sketch, "E71.anchor2", {"start": v(-77.09, -3.64) * mm, "end": v(-64.03, -3.64) * mm, "construction": true});
            skPoint(sketch, "E72.visualSharp", {"position": v(-86.02, 7.41) * mm});
            skPoint(sketch, "E73.visualSharp", {"position": v(-87.02, 6.48) * mm});
            skLineSegment(sketch, "E74.1.0", {"start": v(-77.09, -3.64) * mm, "end": v(-83.87, 8.25) * mm});
            skLineSegment(sketch, "E74.1.1", {"start": v(-77.09, -3.64) * mm, "end": v(-84.98, 7.54) * mm});
            skArc(sketch, "E74.1.2", {"start": v(-83.87, 8.25) * mm, "mid": v(-84.19, 8.5) * mm, "end": v(-84.58, 8.42) * mm});
            skEllipticalArc(sketch, "E74.1.3", {});
            skArc(sketch, "E74.1.4", {"start": v(-84.85, 8.24) * mm, "mid": v(-85.06, 7.92) * mm, "end": v(-84.98, 7.54) * mm});
            skLineSegment(sketch, "E74.2.0", {"start": v(-77.09, -3.64) * mm, "end": v(-81.87, 9.19) * mm});
            skLineSegment(sketch, "E74.2.1", {"start": v(-77.09, -3.64) * mm, "end": v(-83.07, 8.67) * mm});
            skArc(sketch, "E74.2.2", {"start": v(-81.87, 9.19) * mm, "mid": v(-82.14, 9.47) * mm, "end": v(-82.54, 9.47) * mm});
            skEllipticalArc(sketch, "E74.2.3", {});
            skArc(sketch, "E74.2.4", {"start": v(-82.84, 9.34) * mm, "mid": v(-83.1, 9.05) * mm, "end": v(-83.07, 8.67) * mm});
            skLineSegment(sketch, "E74.3.0", {"start": v(-77.09, -3.64) * mm, "end": v(-79.74, 9.79) * mm});
            skLineSegment(sketch, "E74.3.1", {"start": v(-77.09, -3.64) * mm, "end": v(-81.02, 9.47) * mm});
            skArc(sketch, "E74.3.2", {"start": v(-79.74, 9.79) * mm, "mid": v(-79.97, 10.12) * mm, "end": v(-80.36, 10.18) * mm});
            skEllipticalArc(sketch, "E74.3.3", {});
            skArc(sketch, "E74.3.4", {"start": v(-80.67, 10.1) * mm, "mid": v(-80.97, 9.85) * mm, "end": v(-81.02, 9.47) * mm});
            skLineSegment(sketch, "E74.4.0", {"start": v(-77.09, -3.64) * mm, "end": v(-77.55, 10.04) * mm});
            skLineSegment(sketch, "E74.4.1", {"start": v(-77.09, -3.64) * mm, "end": v(-78.86, 9.93) * mm});
            skArc(sketch, "E74.4.2", {"start": v(-77.55, 10.04) * mm, "mid": v(-77.71, 10.4) * mm, "end": v(-78.1, 10.52) * mm});
            skEllipticalArc(sketch, "E74.4.3", {});
            skArc(sketch, "E74.4.4", {"start": v(-78.42, 10.49) * mm, "mid": v(-78.75, 10.3) * mm, "end": v(-78.86, 9.93) * mm});
            skLineSegment(sketch, "E74.5.0", {"start": v(-77.09, -3.64) * mm, "end": v(-75.34, 9.94) * mm});
            skLineSegment(sketch, "E74.5.1", {"start": v(-77.09, -3.64) * mm, "end": v(-76.65, 10.04) * mm});
            skArc(sketch, "E74.5.2", {"start": v(-75.34, 9.94) * mm, "mid": v(-75.45, 10.32) * mm, "end": v(-75.8, 10.5) * mm});
            skEllipticalArc(sketch, "E74.5.3", {});
            skArc(sketch, "E74.5.4", {"start": v(-76.12, 10.52) * mm, "mid": v(-76.49, 10.39) * mm, "end": v(-76.65, 10.04) * mm});
            skLineSegment(sketch, "E74.6.0", {"start": v(-77.09, -3.64) * mm, "end": v(-73.18, 9.48) * mm});
            skLineSegment(sketch, "E74.6.1", {"start": v(-77.09, -3.64) * mm, "end": v(-74.45, 9.79) * mm});
            skArc(sketch, "E74.6.2", {"start": v(-73.18, 9.48) * mm, "mid": v(-73.22, 9.87) * mm, "end": v(-73.54, 10.1) * mm});
            skEllipticalArc(sketch, "E74.6.3", {});
            skArc(sketch, "E74.6.4", {"start": v(-73.86, 10.18) * mm, "mid": v(-74.24, 10.1) * mm, "end": v(-74.45, 9.79) * mm});
            skLineSegment(sketch, "E74.7.0", {"start": v(-77.09, -3.64) * mm, "end": v(-71.12, 8.68) * mm});
            skLineSegment(sketch, "E74.7.1", {"start": v(-77.09, -3.64) * mm, "end": v(-72.33, 9.19) * mm});
            skArc(sketch, "E74.7.2", {"start": v(-71.12, 8.68) * mm, "mid": v(-71.1, 9.07) * mm, "end": v(-71.37, 9.36) * mm});
            skEllipticalArc(sketch, "E74.7.3", {});
            skArc(sketch, "E74.7.4", {"start": v(-71.68, 9.48) * mm, "mid": v(-72.06, 9.47) * mm, "end": v(-72.33, 9.19) * mm});
            skLineSegment(sketch, "E74.8.0", {"start": v(-77.09, -3.64) * mm, "end": v(-69.21, 7.56) * mm});
            skLineSegment(sketch, "E74.8.1", {"start": v(-77.09, -3.64) * mm, "end": v(-70.33, 8.25) * mm});
            skArc(sketch, "E74.8.2", {"start": v(-69.21, 7.56) * mm, "mid": v(-69.13, 7.94) * mm, "end": v(-69.36, 8.27) * mm});
            skEllipticalArc(sketch, "E74.8.3", {});
            skArc(sketch, "E74.8.4", {"start": v(-69.64, 8.44) * mm, "mid": v(-70.02, 8.5) * mm, "end": v(-70.33, 8.25) * mm});
            skPoint(sketch, "E75.1.0.0", {"position": v(-57.78, -3.64) * mm});
            skLineSegment(sketch, "E75.1.0.1", {"start": v(-57.78, -3.64) * mm, "end": v(-51.81, 8.68) * mm});
            skLineSegment(sketch, "E75.1.0.2", {"start": v(-57.78, -3.64) * mm, "end": v(-62.56, 9.19) * mm});
            skLineSegment(sketch, "E75.1.0.3", {"start": v(-57.78, -3.64) * mm, "end": v(-57.34, 10.04) * mm});
            skLineSegment(sketch, "E75.1.0.4", {"start": v(-57.78, -3.64) * mm, "end": v(-51.02, 8.25) * mm});
            skLineSegment(sketch, "E75.1.0.5", {"start": v(-57.78, -3.64) * mm, "end": v(-55.15, 9.79) * mm});
            skLineSegment(sketch, "E75.1.0.6", {"start": v(-57.78, -3.64) * mm, "end": v(-49.9, 7.56) * mm});
            skLineSegment(sketch, "E75.1.0.7", {"start": v(-57.78, -3.64) * mm, "end": v(-58.24, 10.04) * mm});
            skLineSegment(sketch, "E75.1.0.8", {"start": v(-57.78, -3.64) * mm, "end": v(-53.02, 9.19) * mm});
            skLineSegment(sketch, "E75.1.0.9", {"start": v(-57.78, -3.64) * mm, "end": v(-65.67, 7.54) * mm});
            skLineSegment(sketch, "E75.1.0.10", {"start": v(-57.78, -3.64) * mm, "end": v(-53.87, 9.48) * mm});
            skLineSegment(sketch, "E75.1.0.11", {"start": v(-57.78, -3.64) * mm, "end": v(-60.44, 9.79) * mm});
            skLineSegment(sketch, "E75.1.0.12", {"start": v(-57.78, -3.64) * mm, "end": v(-61.7, 9.47) * mm});
            skLineSegment(sketch, "E75.1.0.13", {"start": v(-57.78, -3.64) * mm, "end": v(-56.03, 9.94) * mm});
            skLineSegment(sketch, "E75.1.0.14", {"start": v(-57.78, -3.64) * mm, "end": v(-63.77, 8.67) * mm});
            skLineSegment(sketch, "E75.1.0.15", {"start": v(-57.78, -3.64) * mm, "end": v(-59.55, 9.93) * mm});
            skLineSegment(sketch, "E75.1.0.16", {"start": v(-57.78, -3.64) * mm, "end": v(-64.56, 8.25) * mm});
            skPoint(sketch, "E75.1.0.17", {"position": v(-57.78, -3.64) * mm});
            skArc(sketch, "E75.1.0.18", {"start": v(-52.37, 9.48) * mm, "mid": v(-52.76, 9.47) * mm, "end": v(-53.02, 9.19) * mm});
            skEllipticalArc(sketch, "E75.1.0.19", {});
            skArc(sketch, "E75.1.0.20", {"start": v(-65.54, 8.24) * mm, "mid": v(-65.75, 7.92) * mm, "end": v(-65.67, 7.54) * mm});
            skEllipticalArc(sketch, "E75.1.0.21", {});
            skArc(sketch, "E75.1.0.22", {"start": v(-64.56, 8.25) * mm, "mid": v(-64.88, 8.5) * mm, "end": v(-65.27, 8.42) * mm});
            skArc(sketch, "E75.1.0.23", {"start": v(-51.81, 8.68) * mm, "mid": v(-51.8, 9.07) * mm, "end": v(-52.07, 9.36) * mm});
            skArc(sketch, "E75.1.0.24", {"start": v(-60.44, 9.79) * mm, "mid": v(-60.66, 10.12) * mm, "end": v(-61.05, 10.18) * mm});
            skArc(sketch, "E75.1.0.25", {"start": v(-62.56, 9.19) * mm, "mid": v(-62.84, 9.47) * mm, "end": v(-63.23, 9.47) * mm});
            skArc(sketch, "E75.1.0.26", {"start": v(-53.87, 9.48) * mm, "mid": v(-53.92, 9.87) * mm, "end": v(-54.23, 10.1) * mm});
            skEllipticalArc(sketch, "E75.1.0.27", {});
            skEllipticalArc(sketch, "E75.1.0.28", {});
            skArc(sketch, "E75.1.0.29", {"start": v(-54.55, 10.18) * mm, "mid": v(-54.93, 10.1) * mm, "end": v(-55.15, 9.79) * mm});
            skArc(sketch, "E75.1.0.30", {"start": v(-59.1, 10.49) * mm, "mid": v(-59.45, 10.3) * mm, "end": v(-59.55, 9.93) * mm});
            skArc(sketch, "E75.1.0.31", {"start": v(-56.03, 9.94) * mm, "mid": v(-56.14, 10.32) * mm, "end": v(-56.5, 10.5) * mm});
            skEllipticalArc(sketch, "E75.1.0.32", {});
            skArc(sketch, "E75.1.0.33", {"start": v(-61.37, 10.1) * mm, "mid": v(-61.67, 9.85) * mm, "end": v(-61.7, 9.47) * mm});
            skEllipticalArc(sketch, "E75.1.0.34", {});
            skArc(sketch, "E75.1.0.35", {"start": v(-50.33, 8.44) * mm, "mid": v(-50.71, 8.5) * mm, "end": v(-51.02, 8.25) * mm});
            skArc(sketch, "E75.1.0.36", {"start": v(-56.82, 10.52) * mm, "mid": v(-57.18, 10.39) * mm, "end": v(-57.34, 10.04) * mm});
            skArc(sketch, "E75.1.0.37", {"start": v(-58.24, 10.04) * mm, "mid": v(-58.4, 10.4) * mm, "end": v(-58.78, 10.52) * mm});
            skArc(sketch, "E75.1.0.38", {"start": v(-49.9, 7.56) * mm, "mid": v(-49.82, 7.94) * mm, "end": v(-50.05, 8.27) * mm});
            skArc(sketch, "E75.1.0.39", {"start": v(-63.53, 9.34) * mm, "mid": v(-63.79, 9.05) * mm, "end": v(-63.77, 8.67) * mm});
            skEllipticalArc(sketch, "E75.1.0.40", {});
            skPoint(sketch, "E75.2.0.0", {"position": v(-38.48, -3.64) * mm});
            skLineSegment(sketch, "E75.2.0.1", {"start": v(-38.48, -3.64) * mm, "end": v(-32.5, 8.68) * mm});
            skLineSegment(sketch, "E75.2.0.2", {"start": v(-38.48, -3.64) * mm, "end": v(-43.26, 9.19) * mm});
            skLineSegment(sketch, "E75.2.0.3", {"start": v(-38.48, -3.64) * mm, "end": v(-38.04, 10.04) * mm});
            skLineSegment(sketch, "E75.2.0.4", {"start": v(-38.48, -3.64) * mm, "end": v(-31.71, 8.25) * mm});
            skLineSegment(sketch, "E75.2.0.5", {"start": v(-38.48, -3.64) * mm, "end": v(-35.84, 9.79) * mm});
            skLineSegment(sketch, "E75.2.0.6", {"start": v(-38.48, -3.64) * mm, "end": v(-30.6, 7.56) * mm});
            skLineSegment(sketch, "E75.2.0.7", {"start": v(-38.48, -3.64) * mm, "end": v(-38.93, 10.04) * mm});
            skLineSegment(sketch, "E75.2.0.8", {"start": v(-38.48, -3.64) * mm, "end": v(-33.71, 9.19) * mm});
            skLineSegment(sketch, "E75.2.0.9", {"start": v(-38.48, -3.64) * mm, "end": v(-46.36, 7.54) * mm});
            skLineSegment(sketch, "E75.2.0.10", {"start": v(-38.48, -3.64) * mm, "end": v(-34.56, 9.48) * mm});
            skLineSegment(sketch, "E75.2.0.11", {"start": v(-38.48, -3.64) * mm, "end": v(-41.13, 9.79) * mm});
            skLineSegment(sketch, "E75.2.0.12", {"start": v(-38.48, -3.64) * mm, "end": v(-42.4, 9.47) * mm});
            skLineSegment(sketch, "E75.2.0.13", {"start": v(-38.48, -3.64) * mm, "end": v(-36.73, 9.94) * mm});
            skLineSegment(sketch, "E75.2.0.14", {"start": v(-38.48, -3.64) * mm, "end": v(-44.46, 8.67) * mm});
            skLineSegment(sketch, "E75.2.0.15", {"start": v(-38.48, -3.64) * mm, "end": v(-40.24, 9.93) * mm});
            skLineSegment(sketch, "E75.2.0.16", {"start": v(-38.48, -3.64) * mm, "end": v(-45.26, 8.25) * mm});
            skPoint(sketch, "E75.2.0.17", {"position": v(-38.48, -3.64) * mm});
            skArc(sketch, "E75.2.0.18", {"start": v(-33.06, 9.48) * mm, "mid": v(-33.45, 9.47) * mm, "end": v(-33.71, 9.19) * mm});
            skEllipticalArc(sketch, "E75.2.0.19", {});
            skArc(sketch, "E75.2.0.20", {"start": v(-46.24, 8.24) * mm, "mid": v(-46.45, 7.92) * mm, "end": v(-46.36, 7.54) * mm});
            skEllipticalArc(sketch, "E75.2.0.21", {});
            skArc(sketch, "E75.2.0.22", {"start": v(-45.26, 8.25) * mm, "mid": v(-45.57, 8.5) * mm, "end": v(-45.96, 8.42) * mm});
            skArc(sketch, "E75.2.0.23", {"start": v(-32.5, 8.68) * mm, "mid": v(-32.49, 9.07) * mm, "end": v(-32.76, 9.36) * mm});
            skArc(sketch, "E75.2.0.24", {"start": v(-41.13, 9.79) * mm, "mid": v(-41.35, 10.12) * mm, "end": v(-41.74, 10.18) * mm});
            skArc(sketch, "E75.2.0.25", {"start": v(-43.26, 9.19) * mm, "mid": v(-43.53, 9.47) * mm, "end": v(-43.92, 9.47) * mm});
            skArc(sketch, "E75.2.0.26", {"start": v(-34.56, 9.48) * mm, "mid": v(-34.6, 9.87) * mm, "end": v(-34.93, 10.1) * mm});
            skEllipticalArc(sketch, "E75.2.0.27", {});
            skEllipticalArc(sketch, "E75.2.0.28", {});
            skArc(sketch, "E75.2.0.29", {"start": v(-35.25, 10.18) * mm, "mid": v(-35.63, 10.1) * mm, "end": v(-35.84, 9.79) * mm});
            skArc(sketch, "E75.2.0.30", {"start": v(-39.8, 10.49) * mm, "mid": v(-40.14, 10.3) * mm, "end": v(-40.24, 9.93) * mm});
            skArc(sketch, "E75.2.0.31", {"start": v(-36.73, 9.94) * mm, "mid": v(-36.83, 10.32) * mm, "end": v(-37.19, 10.5) * mm});
            skEllipticalArc(sketch, "E75.2.0.32", {});
            skArc(sketch, "E75.2.0.33", {"start": v(-42.06, 10.1) * mm, "mid": v(-42.36, 9.85) * mm, "end": v(-42.4, 9.47) * mm});
            skEllipticalArc(sketch, "E75.2.0.34", {});
            skArc(sketch, "E75.2.0.35", {"start": v(-31.02, 8.44) * mm, "mid": v(-31.4, 8.5) * mm, "end": v(-31.71, 8.25) * mm});
            skArc(sketch, "E75.2.0.36", {"start": v(-37.51, 10.52) * mm, "mid": v(-37.87, 10.39) * mm, "end": v(-38.04, 10.04) * mm});
            skArc(sketch, "E75.2.0.37", {"start": v(-38.93, 10.04) * mm, "mid": v(-39.1, 10.4) * mm, "end": v(-39.48, 10.52) * mm});
            skArc(sketch, "E75.2.0.38", {"start": v(-30.6, 7.56) * mm, "mid": v(-30.52, 7.94) * mm, "end": v(-30.74, 8.27) * mm});
            skArc(sketch, "E75.2.0.39", {"start": v(-44.22, 9.34) * mm, "mid": v(-44.48, 9.05) * mm, "end": v(-44.46, 8.67) * mm});
            skEllipticalArc(sketch, "E75.2.0.40", {});
            skLineSegment(sketch, "E75.direction1", {"start": v(-77.09, -3.64) * mm, "end": v(-57.78, -3.64) * mm, "construction": true});
            skLineSegment(sketch, "E76", {"start": v(-59.1, 10.49) * mm, "end": v(-58.78, 10.52) * mm});
            skLineSegment(sketch, "E77", {"start": v(-39.8, 10.49) * mm, "end": v(-39.48, 10.52) * mm});
            const initialGuessF17  = {"E64.0": [-0.09612256447526175, -0.0013360511020651194, 0, 1, 0.014, 0.013965054578359462, 0.7180546312957505, 0.7398930087092236], "E70.1.3": [-0.09612256447526175, -0.0013360511020651198, 0.16086763624185027, 0.9869759893786473, 0.014, 0.013965054578359462, 0.718054631295751, 0.7398930087092235], "E70.2.3": [-0.09612256447526175, -0.001336051102065118, 0.317544988877609, 0.9482432072199195, 0.014, 0.013965054578359462, 0.718054631295751, 0.7398930087092231], "E70.3.3": [-0.09612256447526175, -0.001336051102065118, 0.4659509228975692, 0.8848105658562762, 0.014, 0.013965054578359462, 0.718054631295751, 0.7398930087092234], "E70.4.3": [-0.09612256447526175, -0.001336051102065118, 0.6022197573798352, 0.7983303600774383, 0.014, 0.01396505457835946, 0.7180546312957504, 0.739893008709224], "E70.5.3": [-0.09612256447526175, -0.0013360511020651194, 0.722801958829093, 0.6910552281206084, 0.014, 0.013965054578359462, 0.718054631295748, 0.7398930087092209], "E70.6.3": [-0.09612256447526175, -0.0013360511020651194, 0.8245565995005028, 0.5657794749018097, 0.014, 0.013965054578359462, 0.7180546312957475, 0.7398930087092203], "E70.7.3": [-0.09612256447526175, -0.0013360511020651194, 0.904833172352311, 0.4257662859020819, 0.014, 0.013965054578359462, 0.718054631295746, 0.7398930087092198], "E70.8.3": [-0.09612256447526175, -0.0013360511020651194, 0.9615406315095817, 0.2746627276427487, 0.014, 0.013965054578359462, 0.7180546312957461, 0.7398930087092197], "E70.9.3": [-0.09612256447526175, -0.0013360511020651194, 0.9932018598715668, 0.11640474881919785, 0.014, 0.013965054578359462, 0.7180546312957454, 0.7398930087092193], "E74.1.3": [-0.07708931073374041, -0.003644061778911401, 0.160867636241799, 0.9869759893786557, 0.014323932052886448, 0.014046620573596253, 0.7265398216981758, 0.7495844923670351], "E74.2.3": [-0.07708931075018732, -0.0036440627026220612, 0.3175448508741828, 0.9482432534341034, 0.014323932052886448, 0.014046620573596253, 0.7265398216981759, 0.7495844923670342], "E74.3.3": [-0.07708931091501504, -0.0036440636116565443, 0.4659506653542021, 0.8848107014813827, 0.014323932052886448, 0.014046620573596253, 0.726539821698176, 0.749584492367036], "E74.4.3": [-0.07708931122393015, -0.003644064482336354, 0.602219408822693, 0.7983306230110719, 0.014323932052886448, 0.014046620573596253, 0.7265398216981779, 0.7495844923670363], "E74.5.3": [-0.07708931166888604, -0.0036440652919820377, 0.7228015565357182, 0.6910556488948941, 0.014323932052886448, 0.014046620573596253, 0.7265398216981772, 0.7495844923670363], "E74.6.3": [-0.07708931223829249, -0.003644066019503976, 0.8245561877942955, 0.5657800749143952, 0.014323932052886448, 0.014046620573596253, 0.7265398216981775, 0.749584492367036], "E74.7.3": [-0.07708931291731765, -0.0036440666459516824, 0.9048328005664158, 0.4257670760159087, 0.014323932052886448, 0.014046620573596253, 0.7265398216981768, 0.7495844923670354], "E74.8.3": [-0.07708931368827424, -0.003644067155007466, 0.9615403516961704, 0.27466370721303013, 0.014323932052886448, 0.014046620573596253, 0.7265398216981767, 0.7495844923670362], "E75.1.0.19": [-0.057782832917317645, -0.0036440666459516824, 0.904832800566416, 0.4257670760159088, 0.014323932052886448, 0.014046620573596253, 0.7265398216981768, 0.7495844923670354], "E75.1.0.21": [-0.05778283073374041, -0.003644061778911401, 0.160867636241799, 0.9869759893786557, 0.014323932052886448, 0.014046620573596253, 0.7265398216981755, 0.7495844923670351], "E75.1.0.27": [-0.05778283166888604, -0.0036440652919820377, 0.7228015565357182, 0.6910556488948941, 0.014323932052886448, 0.014046620573596253, 0.7265398216981772, 0.7495844923670363], "E75.1.0.28": [-0.05778283091501504, -0.0036440636116565443, 0.4659506653542021, 0.8848107014813827, 0.014323932052886448, 0.014046620573596253, 0.726539821698176, 0.749584492367036], "E75.1.0.32": [-0.057782833688274235, -0.003644067155007466, 0.9615403516961704, 0.27466370721303013, 0.014323932052886448, 0.014046620573596253, 0.7265398216981767, 0.7495844923670362], "E75.1.0.34": [-0.05778283075018732, -0.0036440627026220612, 0.3175448508741828, 0.9482432534341034, 0.014323932052886448, 0.014046620573596253, 0.7265398216981759, 0.7495844923670342], "E75.1.0.40": [-0.05778283223829249, -0.003644066019503976, 0.8245561877942955, 0.5657800749143952, 0.014323932052886448, 0.014046620573596253, 0.7265398216981775, 0.749584492367036], "E75.2.0.19": [-0.038476352917317644, -0.0036440666459516824, 0.904832800566416, 0.4257670760159088, 0.014323932052886448, 0.014046620573596253, 0.7265398216981768, 0.7495844923670354], "E75.2.0.21": [-0.03847635073374041, -0.003644061778911401, 0.160867636241799, 0.9869759893786557, 0.014323932052886448, 0.014046620573596253, 0.7265398216981755, 0.7495844923670351], "E75.2.0.27": [-0.038476351668886036, -0.0036440652919820377, 0.7228015565357182, 0.6910556488948941, 0.014323932052886448, 0.014046620573596253, 0.7265398216981772, 0.7495844923670363], "E75.2.0.28": [-0.03847635091501504, -0.0036440636116565443, 0.4659506653542021, 0.8848107014813827, 0.014323932052886448, 0.014046620573596253, 0.726539821698176, 0.749584492367036], "E75.2.0.32": [-0.038476353688274234, -0.003644067155007466, 0.9615403516961704, 0.27466370721303013, 0.014323932052886448, 0.014046620573596253, 0.7265398216981767, 0.7495844923670362], "E75.2.0.34": [-0.03847635075018732, -0.0036440627026220612, 0.3175448508741828, 0.9482432534341034, 0.014323932052886448, 0.014046620573596253, 0.7265398216981759, 0.7495844923670342], "E75.2.0.40": [-0.03847635223829249, -0.003644066019503976, 0.8245561877942955, 0.5657800749143952, 0.014323932052886448, 0.014046620573596253, 0.7265398216981775, 0.749584492367036]};
            skSetInitialGuess(sketch, initialGuessF17);
            skSolve(sketch);
        }
        {
            var Q0;
            Q0 = qSketchRegion(id + "F17", true);
            extrude(context, id + "F18", {"entities" : qUnion([Q0]), "operationType" : NewBodyOperationType.REMOVE, "endBound" : BoundingType.SYMMETRIC, "oppositeDirection" : true, "depth" : 40 * mm});
        }
        {
            var Q0;
            Q0=makeQuery(id+"F1.opExtrude","SWEPT_FACE",FACE,{"disambiguationData":[OSD([sQuery(id+"F0.wireOp",EDGE,"E21.MirrorCS")])]});
            var sketch = newSketch(context, id + "F19", { "sketchPlane" : qUnion([Q0])});
            skLineSegment(sketch, "E78", {"start": v(-182.27, 9.85) * mm, "end": v(-182.27, 5.5) * mm});
            skLineSegment(sketch, "E79", {"start": v(-182.27, 5.5) * mm, "end": v(-221.62, 5.5) * mm});
            skLineSegment(sketch, "E80", {"start": v(-221.62, 5.5) * mm, "end": v(-221.62, 9.85) * mm});
            skLineSegment(sketch, "E81", {"start": v(-221.62, 9.85) * mm, "end": v(-182.27, 9.85) * mm});
            skSolve(sketch);
        }
        {
            var Q0;
            Q0=makeQuery(id+"F19.imprint","IMPRINT",FACE,{"disambiguationData":[TD([[makeQuery(id+"F19.imprint","IMPRINT",EDGE,{"derivedFrom":sQuery(id+"F19.wireOp",EDGE,"E78")}),-1.0]])]});
            extrude(context, id + "F20", {"entities" : qUnion([Q0]), "endBound" : BoundingType.SYMMETRIC, "depth" : 30 * mm});
        }
        {
            var Q0;
            Q0=makeQuery(id+"F1.opExtrude","SWEPT_BODY",BODY,{"disambiguationData":[OSD([sQuery(id+"F0.wireOp",EDGE,"E1"),sQuery(id+"F0.wireOp",EDGE,"E8"),sQuery(id+"F0.wireOp",EDGE,"E9"),sQuery(id+"F0.wireOp",EDGE,"E10"),sQuery(id+"F0.wireOp",EDGE,"E11"),sQuery(id+"F0.wireOp",EDGE,"E12"),sQuery(id+"F0.wireOp",EDGE,"E13"),sQuery(id+"F0.wireOp",EDGE,"E14"),sQuery(id+"F0.wireOp",EDGE,"E15"),sQuery(id+"F0.wireOp",EDGE,"E16.MirrorCS"),sQuery(id+"F0.wireOp",EDGE,"E17.MirrorCS"),sQuery(id+"F0.wireOp",EDGE,"E18.MirrorCS"),sQuery(id+"F0.wireOp",EDGE,"E19.MirrorCS"),sQuery(id+"F0.wireOp",EDGE,"E20.MirrorCS"),sQuery(id+"F0.wireOp",EDGE,"E21.MirrorCS"),sQuery(id+"F0.wireOp",EDGE,"E22.MirrorCS"),sQuery(id+"F0.wireOp",EDGE,"E23.MirrorCS"),sQuery(id+"F0.wireOp",EDGE,"E24.MirrorCS")])]});
            var Q1;
            Q1=makeQuery(id+"F20.opExtrude","SWEPT_BODY",BODY,{"disambiguationData":[OSD([sQuery(id+"F19.wireOp",EDGE,"E78"),sQuery(id+"F19.wireOp",EDGE,"E79"),sQuery(id+"F19.wireOp",EDGE,"E80"),sQuery(id+"F19.wireOp",EDGE,"E81")])]});
            booleanBodies(context, id + "F21", {"operationType" : BooleanOperationType.INTERSECTION, "tools" : qUnion([Q0, Q1]), "keepTools" : true});
        }
        {
            var Q0;
            Q0=makeQuery(id+"F21.opBoolean","INTERSECT",BODY,{"derivedFrom":[makeQuery(id+"F1.opExtrude","SWEPT_BODY",BODY,{"disambiguationData":[OSD([sQuery(id+"F0.wireOp",EDGE,"E1"),sQuery(id+"F0.wireOp",EDGE,"E8"),sQuery(id+"F0.wireOp",EDGE,"E9"),sQuery(id+"F0.wireOp",EDGE,"E10"),sQuery(id+"F0.wireOp",EDGE,"E11"),sQuery(id+"F0.wireOp",EDGE,"E12"),sQuery(id+"F0.wireOp",EDGE,"E13"),sQuery(id+"F0.wireOp",EDGE,"E14"),sQuery(id+"F0.wireOp",EDGE,"E15"),sQuery(id+"F0.wireOp",EDGE,"E16.MirrorCS"),sQuery(id+"F0.wireOp",EDGE,"E17.MirrorCS"),sQuery(id+"F0.wireOp",EDGE,"E18.MirrorCS"),sQuery(id+"F0.wireOp",EDGE,"E19.MirrorCS"),sQuery(id+"F0.wireOp",EDGE,"E20.MirrorCS"),sQuery(id+"F0.wireOp",EDGE,"E21.MirrorCS"),sQuery(id+"F0.wireOp",EDGE,"E22.MirrorCS"),sQuery(id+"F0.wireOp",EDGE,"E23.MirrorCS"),sQuery(id+"F0.wireOp",EDGE,"E24.MirrorCS")])]}),makeQuery(id+"F20.opExtrude","SWEPT_BODY",BODY,{"disambiguationData":[OSD([sQuery(id+"F19.wireOp",EDGE,"E78"),sQuery(id+"F19.wireOp",EDGE,"E79"),sQuery(id+"F19.wireOp",EDGE,"E80"),sQuery(id+"F19.wireOp",EDGE,"E81")])]})]});
            var Q1;
            Q1=makeQuery(id+"F1.opExtrude","SWEPT_BODY",BODY,{"disambiguationData":[OSD([sQuery(id+"F0.wireOp",EDGE,"E1"),sQuery(id+"F0.wireOp",EDGE,"E8"),sQuery(id+"F0.wireOp",EDGE,"E9"),sQuery(id+"F0.wireOp",EDGE,"E10"),sQuery(id+"F0.wireOp",EDGE,"E11"),sQuery(id+"F0.wireOp",EDGE,"E12"),sQuery(id+"F0.wireOp",EDGE,"E13"),sQuery(id+"F0.wireOp",EDGE,"E14"),sQuery(id+"F0.wireOp",EDGE,"E15"),sQuery(id+"F0.wireOp",EDGE,"E16.MirrorCS"),sQuery(id+"F0.wireOp",EDGE,"E17.MirrorCS"),sQuery(id+"F0.wireOp",EDGE,"E18.MirrorCS"),sQuery(id+"F0.wireOp",EDGE,"E19.MirrorCS"),sQuery(id+"F0.wireOp",EDGE,"E20.MirrorCS"),sQuery(id+"F0.wireOp",EDGE,"E21.MirrorCS"),sQuery(id+"F0.wireOp",EDGE,"E22.MirrorCS"),sQuery(id+"F0.wireOp",EDGE,"E23.MirrorCS"),sQuery(id+"F0.wireOp",EDGE,"E24.MirrorCS")])]});
            booleanBodies(context, id + "F22", {"operationType" : BooleanOperationType.SUBTRACTION, "tools" : qUnion([Q0]), "targets" : qUnion([Q1]), "keepTools" : true});
        }
        {
            var Q0;
            Q0=makeQuery(id+"F21.opBoolean","COPY",FACE,{"derivedFrom":makeQuery(id+"F3.boolean.opBoolean","COPY",FACE,{"derivedFrom":makeQuery(id+"F3.opExtrude","SWEPT_FACE",FACE,{"disambiguationData":[OSD([sQuery(id+"F2.wireOp",EDGE,"E44")])]})})});
            var sketch = newSketch(context, id + "F23", { "sketchPlane" : qUnion([Q0])});
            skCircle(sketch, "E82.2.0.1", {"center": v(-215.28, 3.65) * mm, "radius": 0.5 * mm});
            skCircle(sketch, "E82.2.0.2", {"center": v(-212.5, 3.65) * mm, "radius": 0.5 * mm});
            skCircle(sketch, "E82.2.0.3", {"center": v(-209.71, 3.65) * mm, "radius": 0.5 * mm});
            skCircle(sketch, "E82.2.0.4", {"center": v(-206.93, 3.65) * mm, "radius": 0.5 * mm});
            skCircle(sketch, "E82.2.0.5", {"center": v(-204.15, 3.65) * mm, "radius": 0.5 * mm});
            skCircle(sketch, "E82.2.0.6", {"center": v(-201.36, 3.65) * mm, "radius": 0.5 * mm});
            skCircle(sketch, "E82.2.0.7", {"center": v(-198.58, 3.65) * mm, "radius": 0.5 * mm});
            skCircle(sketch, "E82.2.0.8", {"center": v(-195.8, 3.65) * mm, "radius": 0.5 * mm});
            skCircle(sketch, "E82.2.0.9", {"center": v(-193.01, 3.65) * mm, "radius": 0.5 * mm});
            skCircle(sketch, "E82.2.0.10", {"center": v(-190.23, 3.65) * mm, "radius": 0.5 * mm});
            skCircle(sketch, "E82.2.0.11", {"center": v(-187.45, 3.65) * mm, "radius": 0.5 * mm});
            skCircle(sketch, "E82.3.0.0", {"center": v(-218.08, 1.23) * mm, "radius": 0.5 * mm});
            skCircle(sketch, "E82.3.0.1", {"center": v(-215.3, 1.23) * mm, "radius": 0.5 * mm});
            skCircle(sketch, "E82.3.0.2", {"center": v(-212.51, 1.23) * mm, "radius": 0.5 * mm});
            skCircle(sketch, "E82.3.0.3", {"center": v(-209.73, 1.23) * mm, "radius": 0.5 * mm});
            skCircle(sketch, "E82.3.0.4", {"center": v(-206.94, 1.23) * mm, "radius": 0.5 * mm});
            skCircle(sketch, "E82.3.0.5", {"center": v(-204.16, 1.23) * mm, "radius": 0.5 * mm});
            skCircle(sketch, "E82.3.0.6", {"center": v(-201.38, 1.23) * mm, "radius": 0.5 * mm});
            skCircle(sketch, "E82.3.0.7", {"center": v(-198.6, 1.23) * mm, "radius": 0.5 * mm});
            skCircle(sketch, "E82.3.0.8", {"center": v(-195.81, 1.23) * mm, "radius": 0.5 * mm});
            skCircle(sketch, "E82.3.0.9", {"center": v(-193.03, 1.23) * mm, "radius": 0.5 * mm});
            skCircle(sketch, "E82.3.0.10", {"center": v(-190.25, 1.23) * mm, "radius": 0.5 * mm});
            skCircle(sketch, "E82.3.0.11", {"center": v(-187.46, 1.23) * mm, "radius": 0.5 * mm});
            skCircle(sketch, "E82.4.0.0", {"center": v(-218.1, -1.2) * mm, "radius": 0.5 * mm});
            skCircle(sketch, "E82.4.0.1", {"center": v(-215.3, -1.2) * mm, "radius": 0.5 * mm});
            skCircle(sketch, "E82.4.0.2", {"center": v(-212.53, -1.2) * mm, "radius": 0.5 * mm});
            skCircle(sketch, "E82.4.0.3", {"center": v(-209.74, -1.2) * mm, "radius": 0.5 * mm});
            skCircle(sketch, "E82.4.0.4", {"center": v(-206.96, -1.2) * mm, "radius": 0.5 * mm});
            skCircle(sketch, "E82.4.0.5", {"center": v(-204.18, -1.2) * mm, "radius": 0.5 * mm});
            skCircle(sketch, "E82.4.0.6", {"center": v(-201.4, -1.2) * mm, "radius": 0.5 * mm});
            skCircle(sketch, "E82.4.0.7", {"center": v(-198.61, -1.2) * mm, "radius": 0.5 * mm});
            skCircle(sketch, "E82.4.0.8", {"center": v(-195.83, -1.2) * mm, "radius": 0.5 * mm});
            skCircle(sketch, "E82.4.0.9", {"center": v(-193.04, -1.2) * mm, "radius": 0.5 * mm});
            skCircle(sketch, "E82.4.0.10", {"center": v(-190.26, -1.2) * mm, "radius": 0.5 * mm});
            skCircle(sketch, "E82.4.0.11", {"center": v(-187.48, -1.2) * mm, "radius": 0.5 * mm});
            skCircle(sketch, "E82.5.0.1", {"center": v(-215.33, -3.62) * mm, "radius": 0.5 * mm});
            skCircle(sketch, "E82.5.0.2", {"center": v(-212.54, -3.62) * mm, "radius": 0.5 * mm});
            skCircle(sketch, "E82.5.0.3", {"center": v(-209.76, -3.62) * mm, "radius": 0.5 * mm});
            skCircle(sketch, "E82.5.0.4", {"center": v(-206.98, -3.62) * mm, "radius": 0.5 * mm});
            skCircle(sketch, "E82.5.0.5", {"center": v(-204.2, -3.62) * mm, "radius": 0.5 * mm});
            skCircle(sketch, "E82.5.0.6", {"center": v(-201.41, -3.62) * mm, "radius": 0.5 * mm});
            skCircle(sketch, "E82.5.0.7", {"center": v(-198.63, -3.62) * mm, "radius": 0.5 * mm});
            skCircle(sketch, "E82.5.0.8", {"center": v(-195.84, -3.62) * mm, "radius": 0.5 * mm});
            skCircle(sketch, "E82.5.0.9", {"center": v(-193.06, -3.62) * mm, "radius": 0.5 * mm});
            skCircle(sketch, "E82.5.0.10", {"center": v(-190.28, -3.62) * mm, "radius": 0.5 * mm});
            skCircle(sketch, "E82.5.0.11", {"center": v(-187.5, -3.62) * mm, "radius": 0.5 * mm});
            skCircle(sketch, "E83", {"center": v(-199.98, 5.12) * mm, "radius": 0.53 * mm});
            skCircle(sketch, "E84", {"center": v(-197.32, 5.26) * mm, "radius": 0.53 * mm});
            skCircle(sketch, "E85", {"center": v(-194.56, 5.64) * mm, "radius": 0.52 * mm});
            skCircle(sketch, "E86", {"center": v(-192.15, 5.67) * mm, "radius": 0.52 * mm});
            skCircle(sketch, "E87", {"center": v(-189.5, 5.2) * mm, "radius": 0.53 * mm});
            skCircle(sketch, "E88", {"center": v(-217.48, 3.14) * mm, "radius": 0.5 * mm});
            skLineSegment(sketch, "E89", {"start": v(-185.17, 0) * mm, "end": v(-221.81, 0.11) * mm, "construction": true});
            skCircle(sketch, "E90.MirrorC", {"center": v(-189.53, -5.17) * mm, "radius": 0.53 * mm});
            skCircle(sketch, "E91.MirrorC", {"center": v(-192.18, -5.63) * mm, "radius": 0.52 * mm});
            skCircle(sketch, "E92.MirrorC", {"center": v(-194.6, -5.58) * mm, "radius": 0.52 * mm});
            skCircle(sketch, "E93.MirrorC", {"center": v(-197.35, -5.19) * mm, "radius": 0.53 * mm});
            skCircle(sketch, "E94.MirrorC", {"center": v(-200, -5.03) * mm, "radius": 0.53 * mm});
            skCircle(sketch, "E95.MirrorC", {"center": v(-217.5, -2.94) * mm, "radius": 0.5 * mm});
            skCircle(sketch, "E96", {"center": v(-213.9, 2.44) * mm, "radius": 0.5 * mm});
            skLineSegment(sketch, "E97", {"start": v(-215.28, 3.65) * mm, "end": v(-212.51, 1.23) * mm, "construction": true});
            skLineSegment(sketch, "E98", {"start": v(-215.3, 1.23) * mm, "end": v(-212.5, 3.65) * mm, "construction": true});
            skCircle(sketch, "E99.1.0.0", {"center": v(-211.1, 2.44) * mm, "radius": 0.5 * mm});
            skCircle(sketch, "E99.2.0.0", {"center": v(-208.3, 2.44) * mm, "radius": 0.5 * mm});
            skCircle(sketch, "E99.3.0.0", {"center": v(-205.5, 2.44) * mm, "radius": 0.5 * mm});
            skCircle(sketch, "E99.4.0.0", {"center": v(-202.7, 2.44) * mm, "radius": 0.5 * mm});
            skCircle(sketch, "E99.5.0.0", {"center": v(-199.9, 2.44) * mm, "radius": 0.5 * mm});
            skCircle(sketch, "E99.6.0.0", {"center": v(-197.1, 2.44) * mm, "radius": 0.5 * mm});
            skCircle(sketch, "E99.7.0.0", {"center": v(-194.3, 2.44) * mm, "radius": 0.5 * mm});
            skCircle(sketch, "E99.8.0.0", {"center": v(-191.5, 2.44) * mm, "radius": 0.5 * mm});
            skCircle(sketch, "E99.9.0.0", {"center": v(-188.7, 2.44) * mm, "radius": 0.5 * mm});
            skCircle(sketch, "E99.10.0.0", {"center": v(-185.9, 2.44) * mm, "radius": 0.5 * mm});
            skLineSegment(sketch, "E99.direction1", {"start": v(-213.9, 2.44) * mm, "end": v(-211.1, 2.44) * mm, "construction": true});
            skCircle(sketch, "E100.1.0.0", {"center": v(-213.93, 0.01) * mm, "radius": 0.5 * mm});
            skCircle(sketch, "E100.1.0.1", {"center": v(-211.13, 0.01) * mm, "radius": 0.5 * mm});
            skCircle(sketch, "E100.1.0.2", {"center": v(-208.34, 0.01) * mm, "radius": 0.5 * mm});
            skCircle(sketch, "E100.1.0.3", {"center": v(-205.54, 0.01) * mm, "radius": 0.5 * mm});
            skCircle(sketch, "E100.1.0.4", {"center": v(-202.74, 0.01) * mm, "radius": 0.5 * mm});
            skCircle(sketch, "E100.1.0.5", {"center": v(-199.94, 0.01) * mm, "radius": 0.5 * mm});
            skCircle(sketch, "E100.1.0.6", {"center": v(-197.14, 0.01) * mm, "radius": 0.5 * mm});
            skCircle(sketch, "E100.1.0.7", {"center": v(-194.34, 0.01) * mm, "radius": 0.5 * mm});
            skCircle(sketch, "E100.1.0.8", {"center": v(-191.54, 0.01) * mm, "radius": 0.5 * mm});
            skCircle(sketch, "E100.1.0.9", {"center": v(-188.74, 0.01) * mm, "radius": 0.5 * mm});
            skCircle(sketch, "E100.1.0.10", {"center": v(-185.95, 0.01) * mm, "radius": 0.5 * mm});
            skCircle(sketch, "E100.2.0.0", {"center": v(-213.97, -2.42) * mm, "radius": 0.5 * mm});
            skCircle(sketch, "E100.2.0.1", {"center": v(-211.17, -2.42) * mm, "radius": 0.5 * mm});
            skCircle(sketch, "E100.2.0.2", {"center": v(-208.37, -2.42) * mm, "radius": 0.5 * mm});
            skCircle(sketch, "E100.2.0.3", {"center": v(-205.58, -2.42) * mm, "radius": 0.5 * mm});
            skCircle(sketch, "E100.2.0.4", {"center": v(-202.78, -2.42) * mm, "radius": 0.5 * mm});
            skCircle(sketch, "E100.2.0.5", {"center": v(-199.98, -2.42) * mm, "radius": 0.5 * mm});
            skCircle(sketch, "E100.2.0.6", {"center": v(-197.18, -2.42) * mm, "radius": 0.5 * mm});
            skCircle(sketch, "E100.2.0.7", {"center": v(-194.38, -2.42) * mm, "radius": 0.5 * mm});
            skCircle(sketch, "E100.2.0.8", {"center": v(-191.58, -2.42) * mm, "radius": 0.5 * mm});
            skCircle(sketch, "E100.2.0.9", {"center": v(-188.78, -2.42) * mm, "radius": 0.5 * mm});
            skCircle(sketch, "E100.2.0.10", {"center": v(-185.99, -2.42) * mm, "radius": 0.5 * mm});
            skLineSegment(sketch, "E100.direction1", {"start": v(-213.9, 2.44) * mm, "end": v(-213.93, 0.01) * mm, "construction": true});
            skCircle(sketch, "E101", {"center": v(-202.7, 4.67) * mm, "radius": 0.5 * mm});
            skCircle(sketch, "E102", {"center": v(-205.5, 4.47) * mm, "radius": 0.5 * mm});
            skCircle(sketch, "E103", {"center": v(-208.3, 4.47) * mm, "radius": 0.5 * mm});
            skCircle(sketch, "E104", {"center": v(-216.69, 0.1) * mm, "radius": 0.51 * mm});
            skCircle(sketch, "E105", {"center": v(-216.67, 2.07) * mm, "radius": 0.54 * mm});
            skCircle(sketch, "E106", {"center": v(-216.67, -1.73) * mm, "radius": 0.54 * mm});
            skCircle(sketch, "E107.MirrorC", {"center": v(-208.32, -4.33) * mm, "radius": 0.5 * mm});
            skCircle(sketch, "E108.MirrorC", {"center": v(-205.52, -4.35) * mm, "radius": 0.5 * mm});
            skCircle(sketch, "E109.MirrorC", {"center": v(-202.73, -4.56) * mm, "radius": 0.5 * mm});
            skSolve(sketch);
        }
        {
            var Q0;
            Q0 = qSketchRegion(id + "F23", true);
            extrude(context, id + "F24", {"entities" : qUnion([Q0]), "operationType" : NewBodyOperationType.ADD, "oppositeDirection" : true, "depth" : 2 * mm});
        }
        {
            var Q0;
            Q0 = qSketchRegion(id + "F23", true);
            extrude(context, id + "F25", {"entities" : qUnion([Q0]), "operationType" : NewBodyOperationType.ADD, "depth" : 10 * mm});
        }
        {
            var Q0;
            Q0=makeQuery(id+"F1.opExtrude","SWEPT_FACE",FACE,{"disambiguationData":[OSD([sQuery(id+"F0.wireOp",EDGE,"E21.MirrorCS")])]});
            var sketch = newSketch(context, id + "F26", { "sketchPlane" : qUnion([Q0])});
            skLineSegment(sketch, "E110", {"start": v(-218.82, 19.3) * mm, "end": v(-210.27, 15.92) * mm});
            skLineSegment(sketch, "E111", {"start": v(-210.27, 15.92) * mm, "end": v(-200.88, 18.87) * mm});
            skLineSegment(sketch, "E112", {"start": v(-200.88, 18.87) * mm, "end": v(-193.28, 16) * mm});
            skLineSegment(sketch, "E113", {"start": v(-193.28, 16) * mm, "end": v(-184.53, 19.67) * mm});
            skLineSegment(sketch, "E114", {"start": v(-184.53, 19.67) * mm, "end": v(-218.82, 19.3) * mm});
            skSolve(sketch);
        }
        {
            var Q0;
            Q0=makeQuery(id+"F26.imprint","IMPRINT",FACE,{"disambiguationData":[TD([[makeQuery(id+"F26.imprint","IMPRINT",EDGE,{"derivedFrom":sQuery(id+"F26.wireOp",EDGE,"E110")}),1.0]])]});
            extrude(context, id + "F27", {"entities" : qUnion([Q0]), "operationType" : NewBodyOperationType.REMOVE, "endBound" : BoundingType.SYMMETRIC, "oppositeDirection" : true, "depth" : 40 * mm});
        }
        {
            var Q0;
            Q0=makeQuery(id+"F20.opExtrude","SWEPT_BODY",BODY,{"disambiguationData":[OSD([sQuery(id+"F19.wireOp",EDGE,"E78"),sQuery(id+"F19.wireOp",EDGE,"E79"),sQuery(id+"F19.wireOp",EDGE,"E80"),sQuery(id+"F19.wireOp",EDGE,"E81")])]});
            deleteBodies(context, id + "F28", {"entities" : qUnion([Q0])});
        }
        {
            var Q0;
            Q0=makeQuery(id+"F14.opExtrude","SWEPT_BODY",BODY,{"disambiguationData":[OSD([sQuery(id+"F13.wireOp",EDGE,"E50"),sQuery(id+"F13.wireOp",EDGE,"E51"),sQuery(id+"F13.wireOp",EDGE,"E52"),sQuery(id+"F13.wireOp",EDGE,"E53"),sQuery(id+"F13.wireOp",EDGE,"E54"),sQuery(id+"F13.wireOp",EDGE,"E55"),sQuery(id+"F13.wireOp",EDGE,"E56"),sQuery(id+"F13.wireOp",EDGE,"E57"),sQuery(id+"F13.wireOp",EDGE,"E58.filletArc"),sQuery(id+"F13.wireOp",EDGE,"E59.filletArc"),sQuery(id+"F13.wireOp",EDGE,"E60.filletArc"),sQuery(id+"F13.wireOp",EDGE,"E61.filletArc"),sQuery(id+"F13.wireOp",EDGE,"E62.filletArc"),sQuery(id+"F13.wireOp",EDGE,"E63")])]});
            deleteBodies(context, id + "F29", {"entities" : qUnion([Q0])});
        }
        {
            var Q0;
            Q0=makeQuery(id+"F1.opExtrude","SWEPT_BODY",BODY,{"disambiguationData":[OSD([sQuery(id+"F0.wireOp",EDGE,"E1"),sQuery(id+"F0.wireOp",EDGE,"E8"),sQuery(id+"F0.wireOp",EDGE,"E9"),sQuery(id+"F0.wireOp",EDGE,"E10"),sQuery(id+"F0.wireOp",EDGE,"E11"),sQuery(id+"F0.wireOp",EDGE,"E12"),sQuery(id+"F0.wireOp",EDGE,"E13"),sQuery(id+"F0.wireOp",EDGE,"E14"),sQuery(id+"F0.wireOp",EDGE,"E15"),sQuery(id+"F0.wireOp",EDGE,"E16.MirrorCS"),sQuery(id+"F0.wireOp",EDGE,"E17.MirrorCS"),sQuery(id+"F0.wireOp",EDGE,"E18.MirrorCS"),sQuery(id+"F0.wireOp",EDGE,"E19.MirrorCS"),sQuery(id+"F0.wireOp",EDGE,"E20.MirrorCS"),sQuery(id+"F0.wireOp",EDGE,"E21.MirrorCS"),sQuery(id+"F0.wireOp",EDGE,"E22.MirrorCS"),sQuery(id+"F0.wireOp",EDGE,"E23.MirrorCS"),sQuery(id+"F0.wireOp",EDGE,"E24.MirrorCS")])]});
            var Q1;
            Q1=makeQuery(id+"F15.opBoolean","INTERSECT",BODY,{"derivedFrom":[makeQuery(id+"F1.opExtrude","SWEPT_BODY",BODY,{"disambiguationData":[OSD([sQuery(id+"F0.wireOp",EDGE,"E1"),sQuery(id+"F0.wireOp",EDGE,"E8"),sQuery(id+"F0.wireOp",EDGE,"E9"),sQuery(id+"F0.wireOp",EDGE,"E10"),sQuery(id+"F0.wireOp",EDGE,"E11"),sQuery(id+"F0.wireOp",EDGE,"E12"),sQuery(id+"F0.wireOp",EDGE,"E13"),sQuery(id+"F0.wireOp",EDGE,"E14"),sQuery(id+"F0.wireOp",EDGE,"E15"),sQuery(id+"F0.wireOp",EDGE,"E16.MirrorCS"),sQuery(id+"F0.wireOp",EDGE,"E17.MirrorCS"),sQuery(id+"F0.wireOp",EDGE,"E18.MirrorCS"),sQuery(id+"F0.wireOp",EDGE,"E19.MirrorCS"),sQuery(id+"F0.wireOp",EDGE,"E20.MirrorCS"),sQuery(id+"F0.wireOp",EDGE,"E21.MirrorCS"),sQuery(id+"F0.wireOp",EDGE,"E22.MirrorCS"),sQuery(id+"F0.wireOp",EDGE,"E23.MirrorCS"),sQuery(id+"F0.wireOp",EDGE,"E24.MirrorCS")])]}),makeQuery(id+"F14.opExtrude","SWEPT_BODY",BODY,{"disambiguationData":[OSD([sQuery(id+"F13.wireOp",EDGE,"E50"),sQuery(id+"F13.wireOp",EDGE,"E51"),sQuery(id+"F13.wireOp",EDGE,"E52"),sQuery(id+"F13.wireOp",EDGE,"E53"),sQuery(id+"F13.wireOp",EDGE,"E54"),sQuery(id+"F13.wireOp",EDGE,"E55"),sQuery(id+"F13.wireOp",EDGE,"E56"),sQuery(id+"F13.wireOp",EDGE,"E57"),sQuery(id+"F13.wireOp",EDGE,"E58.filletArc"),sQuery(id+"F13.wireOp",EDGE,"E59.filletArc"),sQuery(id+"F13.wireOp",EDGE,"E60.filletArc"),sQuery(id+"F13.wireOp",EDGE,"E61.filletArc"),sQuery(id+"F13.wireOp",EDGE,"E62.filletArc"),sQuery(id+"F13.wireOp",EDGE,"E63")])]})]});
            var Q2;
            Q2=makeQuery(id+"F21.opBoolean","INTERSECT",BODY,{"derivedFrom":[makeQuery(id+"F1.opExtrude","SWEPT_BODY",BODY,{"disambiguationData":[OSD([sQuery(id+"F0.wireOp",EDGE,"E1"),sQuery(id+"F0.wireOp",EDGE,"E8"),sQuery(id+"F0.wireOp",EDGE,"E9"),sQuery(id+"F0.wireOp",EDGE,"E10"),sQuery(id+"F0.wireOp",EDGE,"E11"),sQuery(id+"F0.wireOp",EDGE,"E12"),sQuery(id+"F0.wireOp",EDGE,"E13"),sQuery(id+"F0.wireOp",EDGE,"E14"),sQuery(id+"F0.wireOp",EDGE,"E15"),sQuery(id+"F0.wireOp",EDGE,"E16.MirrorCS"),sQuery(id+"F0.wireOp",EDGE,"E17.MirrorCS"),sQuery(id+"F0.wireOp",EDGE,"E18.MirrorCS"),sQuery(id+"F0.wireOp",EDGE,"E19.MirrorCS"),sQuery(id+"F0.wireOp",EDGE,"E20.MirrorCS"),sQuery(id+"F0.wireOp",EDGE,"E21.MirrorCS"),sQuery(id+"F0.wireOp",EDGE,"E22.MirrorCS"),sQuery(id+"F0.wireOp",EDGE,"E23.MirrorCS"),sQuery(id+"F0.wireOp",EDGE,"E24.MirrorCS")])]}),makeQuery(id+"F20.opExtrude","SWEPT_BODY",BODY,{"disambiguationData":[OSD([sQuery(id+"F19.wireOp",EDGE,"E78"),sQuery(id+"F19.wireOp",EDGE,"E79"),sQuery(id+"F19.wireOp",EDGE,"E80"),sQuery(id+"F19.wireOp",EDGE,"E81")])]})]});
            var Q3;
            {var subQ0=sQuery(id+"F0.wireOp",EDGE,"E20.MirrorCS");var subQ1=makeQuery(id+"F1.opExtrude","SWEPT_FACE",FACE,{"disambiguationData":[OSD([subQ0])]});var subQ2=sQuery(id+"F0.wireOp",EDGE,"E21.MirrorCS");var subQ3=sQuery(id+"F2.wireOp",EDGE,"E46");var subQ4=sQuery(id+"F2.wireOp",EDGE,"E45");Q3=makeQuery(id+"F8.opFillet","BLEND_VERTEX",VERTEX,{"blendedFrom":[makeQuery(id+"F4.opFillet","BLEND_EDGE",EDGE,{"blendedFrom":[makeQuery(id+"F3.boolean.opBoolean","COPY",EDGE,{"derivedFrom":makeQuery(id+"F3.opExtrude","SWEPT_EDGE",EDGE,{"disambiguationData":[OSD([subQ0,subQ2,subQ4,subQ3])]})}),subQ1],"blendedInto":[subQ1]}),makeQuery(id+"F6.opFillet","BLEND_EDGE",EDGE,{"blendedFrom":[makeQuery(id+"F1.opExtrude","SWEPT_EDGE",EDGE,{"disambiguationData":[OSD([subQ0,subQ2])]}),makeQuery(id+"F4.opFillet","BLEND_FACE",FACE,{"disambiguationData":[OSD([subQ0,subQ2,subQ4,subQ3])]})],"blendedInto":[makeQuery(id+"F4.opFillet","BLEND_FACE",FACE,{"disambiguationData":[OSD([subQ0,subQ2,subQ4,subQ3])]})]}),makeQuery(id+"F6.opFillet","BLEND_FACE",FACE,{"disambiguationData":[OSD([subQ0,subQ2])]}),subQ1],"blendedInto":[makeQuery(id+"F6.opFillet","BLEND_FACE",FACE,{"disambiguationData":[OSD([subQ0,subQ2])]}),subQ1]});}
            transform(context, id + "F30", {"entities" : qUnion([Q0, Q1, Q2]), "transformType" : TransformType.SCALE_UNIFORMLY, "scale" : .8, "scalePoint" : qUnion([Q3]), "makeCopy" : false});
        }
    });
